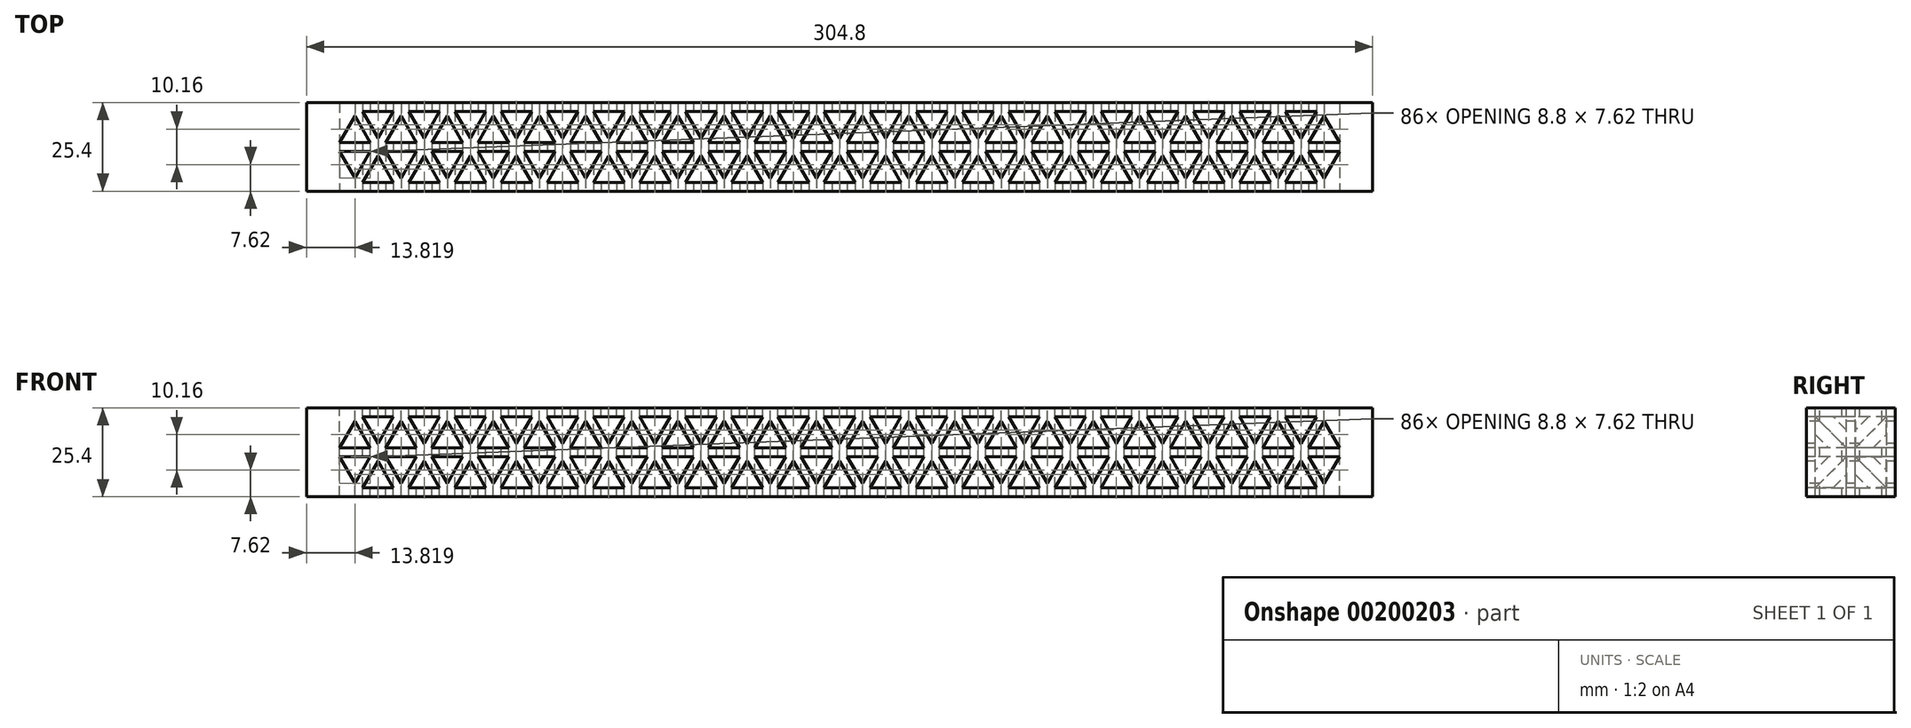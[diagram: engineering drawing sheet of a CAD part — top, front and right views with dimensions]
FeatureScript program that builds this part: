
annotation { "Feature Type Name" : "Feature", "Feature Type Description" : "" }
export const myFeature = defineFeature(function(context is Context, id is Id, definition is map)
    precondition{}
    {
        {
            var Q0;
            Q0=qCreatedBy(makeId("Right.planeOp"),FACE);
            var sketch = newSketch(context, id + "F0", { "sketchPlane" : qUnion([Q0])});
            skLineSegment(sketch, "E0.bottom", {"start": v(12.7, 12.7) * mm, "end": v(-12.7, 12.7) * mm});
            skLineSegment(sketch, "E0.top", {"start": v(12.7, -12.7) * mm, "end": v(-12.7, -12.7) * mm});
            skLineSegment(sketch, "E0.left", {"start": v(12.7, 12.7) * mm, "end": v(12.7, -12.7) * mm});
            skLineSegment(sketch, "E0.right", {"start": v(-12.7, 12.7) * mm, "end": v(-12.7, -12.7) * mm});
            skPoint(sketch, "E0.middle", {"position": v(0, 0) * mm});
            skSolve(sketch);
        }
        {
            var Q0;
            Q0 = qSketchRegion(id + "F0", true);
            extrude(context, id + "F1", {"entities" : qUnion([Q0]), "endBound" : BoundingType.SYMMETRIC, "depth" : 304.8 * mm});
        }
        {
            var Q0;
            Q0=makeQuery(id+"F1.opExtrude","SWEPT_FACE",FACE,{"disambiguationData":[OSD([sQuery(id+"F0.wireOp",EDGE,"E0.right")])]});
            var sketch = newSketch(context, id + "F2", { "sketchPlane" : qUnion([Q0])});
            skCircle(sketch, "E1.cCircle", {"center": v(0, 0) * mm, "radius": 11.43 * mm, "construction": true});
            skLineSegment(sketch, "E1.0", {"start": v(-6.6, 11.43) * mm, "end": v(6.6, 11.43) * mm, "construction": true});
            skLineSegment(sketch, "E1.1", {"start": v(6.6, 11.43) * mm, "end": v(13.2, 0) * mm, "construction": true});
            skLineSegment(sketch, "E1.2", {"start": v(13.2, 0) * mm, "end": v(6.6, -11.43) * mm, "construction": true});
            skLineSegment(sketch, "E1.3", {"start": v(6.6, -11.43) * mm, "end": v(-6.6, -11.43) * mm, "construction": true});
            skLineSegment(sketch, "E1.4", {"start": v(-6.6, -11.43) * mm, "end": v(-13.2, 0) * mm, "construction": true});
            skLineSegment(sketch, "E1.5", {"start": v(-13.2, 0) * mm, "end": v(-6.6, 11.43) * mm, "construction": true});
            skPoint(sketch, "E1.0.midPoint", {"position": v(0, 11.43) * mm});
            skLineSegment(sketch, "E2", {"start": v(6.6, 11.43) * mm, "end": v(-6.6, -11.43) * mm, "construction": true});
            skLineSegment(sketch, "E3", {"start": v(-6.6, 11.43) * mm, "end": v(6.6, -11.43) * mm, "construction": true});
            skLineSegment(sketch, "E4", {"start": v(-13.2, 0) * mm, "end": v(13.2, 0) * mm, "construction": true});
            skLineSegment(sketch, "E5.0", {"start": v(-6.6, -8.9) * mm, "end": v(-11, -1.27) * mm});
            skLineSegment(sketch, "E5.1", {"start": v(-4.4, 10.16) * mm, "end": v(4.4, 10.16) * mm});
            skLineSegment(sketch, "E5.2", {"start": v(6.6, 8.89) * mm, "end": v(11, 1.27) * mm});
            skLineSegment(sketch, "E5.3", {"start": v(-11, 1.27) * mm, "end": v(-6.6, 8.9) * mm});
            skLineSegment(sketch, "E5.4", {"start": v(11, -1.27) * mm, "end": v(6.6, -8.9) * mm});
            skLineSegment(sketch, "E5.5", {"start": v(4.4, -10.16) * mm, "end": v(-4.4, -10.16) * mm});
            skLineSegment(sketch, "E6.0", {"start": v(4.4, 10.16) * mm, "end": v(0, 2.54) * mm});
            skLineSegment(sketch, "E7.0", {"start": v(6.6, 8.9) * mm, "end": v(2.2, 1.27) * mm});
            skLineSegment(sketch, "E8.0", {"start": v(-11, -1.27) * mm, "end": v(-2.2, -1.27) * mm});
            skLineSegment(sketch, "E9.0", {"start": v(-11, 1.27) * mm, "end": v(-2.2, 1.27) * mm});
            skLineSegment(sketch, "E10.trimOffspring", {"start": v(-4.4, 10.16) * mm, "end": v(0, 2.54) * mm});
            skLineSegment(sketch, "E11.trimOffspring", {"start": v(-6.6, 8.9) * mm, "end": v(-2.2, 1.27) * mm});
            skLineSegment(sketch, "E12.trimOffspring", {"start": v(0, -2.54) * mm, "end": v(4.4, -10.16) * mm});
            skLineSegment(sketch, "E13.trimOffspring", {"start": v(2.2, 1.27) * mm, "end": v(11, 1.27) * mm});
            skLineSegment(sketch, "E14.trimOffspring", {"start": v(-2.2, -1.27) * mm, "end": v(-6.6, -8.9) * mm});
            skLineSegment(sketch, "E15.trimOffspring", {"start": v(2.2, -1.27) * mm, "end": v(6.6, -8.9) * mm});
            skLineSegment(sketch, "E16.trimOffspring", {"start": v(0, -2.54) * mm, "end": v(-4.4, -10.16) * mm});
            skLineSegment(sketch, "E17.trimOffspring", {"start": v(2.2, -1.27) * mm, "end": v(11, -1.27) * mm});
            skLineSegment(sketch, "E18.1.0.0", {"start": v(-24.2, 1.27) * mm, "end": v(-19.8, 8.89) * mm});
            skLineSegment(sketch, "E18.1.0.1", {"start": v(-19.8, 8.9) * mm, "end": v(-15.4, 1.27) * mm});
            skLineSegment(sketch, "E18.1.0.2", {"start": v(-24.2, 1.27) * mm, "end": v(-15.4, 1.27) * mm});
            skLineSegment(sketch, "E18.1.0.3", {"start": v(-15.4, -1.27) * mm, "end": v(-19.8, -8.9) * mm});
            skLineSegment(sketch, "E18.1.0.4", {"start": v(-24.2, -1.27) * mm, "end": v(-15.4, -1.27) * mm});
            skLineSegment(sketch, "E18.1.0.5", {"start": v(-19.8, -8.9) * mm, "end": v(-24.2, -1.27) * mm});
            skLineSegment(sketch, "E18.1.0.6", {"start": v(-13.2, -2.54) * mm, "end": v(-8.8, -10.16) * mm});
            skLineSegment(sketch, "E18.1.0.7", {"start": v(-13.2, -2.54) * mm, "end": v(-17.6, -10.16) * mm});
            skLineSegment(sketch, "E18.1.0.8", {"start": v(-8.8, -10.16) * mm, "end": v(-17.6, -10.16) * mm});
            skLineSegment(sketch, "E18.1.0.9", {"start": v(-8.8, 10.16) * mm, "end": v(-13.2, 2.54) * mm});
            skLineSegment(sketch, "E18.1.0.10", {"start": v(-17.6, 10.16) * mm, "end": v(-13.2, 2.54) * mm});
            skLineSegment(sketch, "E18.1.0.11", {"start": v(-17.6, 10.16) * mm, "end": v(-8.8, 10.16) * mm});
            skLineSegment(sketch, "E18.2.0.0", {"start": v(-37.4, 1.27) * mm, "end": v(-33, 8.89) * mm});
            skLineSegment(sketch, "E18.2.0.1", {"start": v(-33, 8.9) * mm, "end": v(-28.6, 1.27) * mm});
            skLineSegment(sketch, "E18.2.0.2", {"start": v(-37.4, 1.27) * mm, "end": v(-28.6, 1.27) * mm});
            skLineSegment(sketch, "E18.2.0.3", {"start": v(-28.6, -1.27) * mm, "end": v(-33, -8.9) * mm});
            skLineSegment(sketch, "E18.2.0.4", {"start": v(-37.4, -1.27) * mm, "end": v(-28.6, -1.27) * mm});
            skLineSegment(sketch, "E18.2.0.5", {"start": v(-33, -8.9) * mm, "end": v(-37.4, -1.27) * mm});
            skLineSegment(sketch, "E18.2.0.6", {"start": v(-26.4, -2.54) * mm, "end": v(-22, -10.16) * mm});
            skLineSegment(sketch, "E18.2.0.7", {"start": v(-26.4, -2.54) * mm, "end": v(-30.8, -10.16) * mm});
            skLineSegment(sketch, "E18.2.0.8", {"start": v(-22, -10.16) * mm, "end": v(-30.8, -10.16) * mm});
            skLineSegment(sketch, "E18.2.0.9", {"start": v(-22, 10.16) * mm, "end": v(-26.4, 2.54) * mm});
            skLineSegment(sketch, "E18.2.0.10", {"start": v(-30.8, 10.16) * mm, "end": v(-26.4, 2.54) * mm});
            skLineSegment(sketch, "E18.2.0.11", {"start": v(-30.8, 10.16) * mm, "end": v(-22, 10.16) * mm});
            skLineSegment(sketch, "E18.direction1", {"start": v(-6.6, -8.9) * mm, "end": v(-19.8, -8.9) * mm, "construction": true});
            skLineSegment(sketch, "E19.0.3.0", {"start": v(-50.6, 1.27) * mm, "end": v(-46.2, 8.9) * mm});
            skLineSegment(sketch, "E19.3.3.0", {"start": v(-46.2, 8.9) * mm, "end": v(-41.8, 1.27) * mm});
            skLineSegment(sketch, "E19.6.3.0", {"start": v(-50.6, 1.27) * mm, "end": v(-41.8, 1.27) * mm});
            skLineSegment(sketch, "E19.9.3.0", {"start": v(-41.8, -1.27) * mm, "end": v(-46.2, -8.9) * mm});
            skLineSegment(sketch, "E19.12.3.0", {"start": v(-50.6, -1.27) * mm, "end": v(-41.8, -1.27) * mm});
            skLineSegment(sketch, "E19.15.3.0", {"start": v(-46.2, -8.9) * mm, "end": v(-50.6, -1.27) * mm});
            skLineSegment(sketch, "E19.18.3.0", {"start": v(-39.6, -2.54) * mm, "end": v(-35.2, -10.16) * mm});
            skLineSegment(sketch, "E19.21.3.0", {"start": v(-39.6, -2.54) * mm, "end": v(-44, -10.16) * mm});
            skLineSegment(sketch, "E19.24.3.0", {"start": v(-35.2, -10.16) * mm, "end": v(-44, -10.16) * mm});
            skLineSegment(sketch, "E19.27.3.0", {"start": v(-35.2, 10.16) * mm, "end": v(-39.6, 2.54) * mm});
            skLineSegment(sketch, "E19.30.3.0", {"start": v(-44, 10.16) * mm, "end": v(-39.6, 2.54) * mm});
            skLineSegment(sketch, "E19.33.3.0", {"start": v(-44, 10.16) * mm, "end": v(-35.2, 10.16) * mm});
            skLineSegment(sketch, "E19.0.4.0", {"start": v(-63.8, 1.27) * mm, "end": v(-59.4, 8.9) * mm});
            skLineSegment(sketch, "E19.3.4.0", {"start": v(-59.4, 8.9) * mm, "end": v(-55, 1.27) * mm});
            skLineSegment(sketch, "E19.6.4.0", {"start": v(-63.8, 1.27) * mm, "end": v(-55, 1.27) * mm});
            skLineSegment(sketch, "E19.9.4.0", {"start": v(-55, -1.27) * mm, "end": v(-59.4, -8.9) * mm});
            skLineSegment(sketch, "E19.12.4.0", {"start": v(-63.8, -1.27) * mm, "end": v(-55, -1.27) * mm});
            skLineSegment(sketch, "E19.15.4.0", {"start": v(-59.4, -8.9) * mm, "end": v(-63.8, -1.27) * mm});
            skLineSegment(sketch, "E19.18.4.0", {"start": v(-52.8, -2.54) * mm, "end": v(-48.4, -10.16) * mm});
            skLineSegment(sketch, "E19.21.4.0", {"start": v(-52.8, -2.54) * mm, "end": v(-57.2, -10.16) * mm});
            skLineSegment(sketch, "E19.24.4.0", {"start": v(-48.4, -10.16) * mm, "end": v(-57.2, -10.16) * mm});
            skLineSegment(sketch, "E19.27.4.0", {"start": v(-48.4, 10.16) * mm, "end": v(-52.8, 2.54) * mm});
            skLineSegment(sketch, "E19.30.4.0", {"start": v(-57.2, 10.16) * mm, "end": v(-52.8, 2.54) * mm});
            skLineSegment(sketch, "E19.33.4.0", {"start": v(-57.2, 10.16) * mm, "end": v(-48.4, 10.16) * mm});
            skLineSegment(sketch, "E20.0.5.0", {"start": v(-76.99, 1.27) * mm, "end": v(-72.6, 8.9) * mm});
            skLineSegment(sketch, "E20.3.5.0", {"start": v(-72.6, 8.9) * mm, "end": v(-68.2, 1.27) * mm});
            skLineSegment(sketch, "E20.6.5.0", {"start": v(-76.99, 1.27) * mm, "end": v(-68.2, 1.27) * mm});
            skLineSegment(sketch, "E20.9.5.0", {"start": v(-68.2, -1.27) * mm, "end": v(-72.6, -8.9) * mm});
            skLineSegment(sketch, "E20.12.5.0", {"start": v(-76.99, -1.27) * mm, "end": v(-68.2, -1.27) * mm});
            skLineSegment(sketch, "E20.15.5.0", {"start": v(-72.6, -8.9) * mm, "end": v(-76.99, -1.27) * mm});
            skLineSegment(sketch, "E20.18.5.0", {"start": v(-66, -2.54) * mm, "end": v(-61.6, -10.16) * mm});
            skLineSegment(sketch, "E20.21.5.0", {"start": v(-66, -2.54) * mm, "end": v(-70.4, -10.16) * mm});
            skLineSegment(sketch, "E20.24.5.0", {"start": v(-61.6, -10.16) * mm, "end": v(-70.4, -10.16) * mm});
            skLineSegment(sketch, "E20.27.5.0", {"start": v(-61.6, 10.16) * mm, "end": v(-66, 2.54) * mm});
            skLineSegment(sketch, "E20.30.5.0", {"start": v(-70.4, 10.16) * mm, "end": v(-66, 2.54) * mm});
            skLineSegment(sketch, "E20.33.5.0", {"start": v(-70.4, 10.16) * mm, "end": v(-61.6, 10.16) * mm});
            skLineSegment(sketch, "E20.0.6.0", {"start": v(-90.19, 1.27) * mm, "end": v(-85.79, 8.9) * mm});
            skLineSegment(sketch, "E20.3.6.0", {"start": v(-85.79, 8.9) * mm, "end": v(-81.39, 1.27) * mm});
            skLineSegment(sketch, "E20.6.6.0", {"start": v(-90.19, 1.27) * mm, "end": v(-81.39, 1.27) * mm});
            skLineSegment(sketch, "E20.9.6.0", {"start": v(-81.39, -1.27) * mm, "end": v(-85.79, -8.9) * mm});
            skLineSegment(sketch, "E20.12.6.0", {"start": v(-90.19, -1.27) * mm, "end": v(-81.39, -1.27) * mm});
            skLineSegment(sketch, "E20.15.6.0", {"start": v(-85.79, -8.9) * mm, "end": v(-90.19, -1.27) * mm});
            skLineSegment(sketch, "E20.18.6.0", {"start": v(-79.19, -2.54) * mm, "end": v(-74.79, -10.16) * mm});
            skLineSegment(sketch, "E20.21.6.0", {"start": v(-79.19, -2.54) * mm, "end": v(-83.59, -10.16) * mm});
            skLineSegment(sketch, "E20.24.6.0", {"start": v(-74.79, -10.16) * mm, "end": v(-83.59, -10.16) * mm});
            skLineSegment(sketch, "E20.27.6.0", {"start": v(-74.79, 10.16) * mm, "end": v(-79.19, 2.54) * mm});
            skLineSegment(sketch, "E20.30.6.0", {"start": v(-83.59, 10.16) * mm, "end": v(-79.19, 2.54) * mm});
            skLineSegment(sketch, "E20.33.6.0", {"start": v(-83.59, 10.16) * mm, "end": v(-74.79, 10.16) * mm});
            skLineSegment(sketch, "E20.0.7.0", {"start": v(-103.39, 1.27) * mm, "end": v(-98.99, 8.9) * mm});
            skLineSegment(sketch, "E20.3.7.0", {"start": v(-98.99, 8.9) * mm, "end": v(-94.59, 1.27) * mm});
            skLineSegment(sketch, "E20.6.7.0", {"start": v(-103.39, 1.27) * mm, "end": v(-94.59, 1.27) * mm});
            skLineSegment(sketch, "E20.9.7.0", {"start": v(-94.59, -1.27) * mm, "end": v(-98.99, -8.9) * mm});
            skLineSegment(sketch, "E20.12.7.0", {"start": v(-103.39, -1.27) * mm, "end": v(-94.59, -1.27) * mm});
            skLineSegment(sketch, "E20.15.7.0", {"start": v(-98.99, -8.9) * mm, "end": v(-103.39, -1.27) * mm});
            skLineSegment(sketch, "E20.18.7.0", {"start": v(-92.39, -2.54) * mm, "end": v(-87.99, -10.16) * mm});
            skLineSegment(sketch, "E20.21.7.0", {"start": v(-92.39, -2.54) * mm, "end": v(-96.79, -10.16) * mm});
            skLineSegment(sketch, "E20.24.7.0", {"start": v(-87.99, -10.16) * mm, "end": v(-96.79, -10.16) * mm});
            skLineSegment(sketch, "E20.27.7.0", {"start": v(-87.99, 10.16) * mm, "end": v(-92.39, 2.54) * mm});
            skLineSegment(sketch, "E20.30.7.0", {"start": v(-96.79, 10.16) * mm, "end": v(-92.39, 2.54) * mm});
            skLineSegment(sketch, "E20.33.7.0", {"start": v(-96.79, 10.16) * mm, "end": v(-87.99, 10.16) * mm});
            skLineSegment(sketch, "E20.0.8.0", {"start": v(-116.58, 1.27) * mm, "end": v(-112.18, 8.9) * mm});
            skLineSegment(sketch, "E20.3.8.0", {"start": v(-112.18, 8.9) * mm, "end": v(-107.79, 1.27) * mm});
            skLineSegment(sketch, "E20.6.8.0", {"start": v(-116.58, 1.27) * mm, "end": v(-107.79, 1.27) * mm});
            skLineSegment(sketch, "E20.9.8.0", {"start": v(-107.79, -1.27) * mm, "end": v(-112.18, -8.9) * mm});
            skLineSegment(sketch, "E20.12.8.0", {"start": v(-116.58, -1.27) * mm, "end": v(-107.79, -1.27) * mm});
            skLineSegment(sketch, "E20.15.8.0", {"start": v(-112.18, -8.9) * mm, "end": v(-116.58, -1.27) * mm});
            skLineSegment(sketch, "E20.18.8.0", {"start": v(-105.59, -2.54) * mm, "end": v(-101.19, -10.16) * mm});
            skLineSegment(sketch, "E20.21.8.0", {"start": v(-105.59, -2.54) * mm, "end": v(-109.99, -10.16) * mm});
            skLineSegment(sketch, "E20.24.8.0", {"start": v(-101.19, -10.16) * mm, "end": v(-109.99, -10.16) * mm});
            skLineSegment(sketch, "E20.27.8.0", {"start": v(-101.19, 10.16) * mm, "end": v(-105.59, 2.54) * mm});
            skLineSegment(sketch, "E20.30.8.0", {"start": v(-109.99, 10.16) * mm, "end": v(-105.59, 2.54) * mm});
            skLineSegment(sketch, "E20.33.8.0", {"start": v(-109.99, 10.16) * mm, "end": v(-101.19, 10.16) * mm});
            skLineSegment(sketch, "E20.0.9.0", {"start": v(-129.78, 1.27) * mm, "end": v(-125.38, 8.9) * mm});
            skLineSegment(sketch, "E20.3.9.0", {"start": v(-125.38, 8.9) * mm, "end": v(-120.98, 1.27) * mm});
            skLineSegment(sketch, "E20.6.9.0", {"start": v(-129.78, 1.27) * mm, "end": v(-120.98, 1.27) * mm});
            skLineSegment(sketch, "E20.9.9.0", {"start": v(-120.98, -1.27) * mm, "end": v(-125.38, -8.9) * mm});
            skLineSegment(sketch, "E20.12.9.0", {"start": v(-129.78, -1.27) * mm, "end": v(-120.98, -1.27) * mm});
            skLineSegment(sketch, "E20.15.9.0", {"start": v(-125.38, -8.9) * mm, "end": v(-129.78, -1.27) * mm});
            skLineSegment(sketch, "E20.18.9.0", {"start": v(-118.78, -2.54) * mm, "end": v(-114.38, -10.16) * mm});
            skLineSegment(sketch, "E20.21.9.0", {"start": v(-118.78, -2.54) * mm, "end": v(-123.18, -10.16) * mm});
            skLineSegment(sketch, "E20.24.9.0", {"start": v(-114.38, -10.16) * mm, "end": v(-123.18, -10.16) * mm});
            skLineSegment(sketch, "E20.27.9.0", {"start": v(-114.38, 10.16) * mm, "end": v(-118.78, 2.54) * mm});
            skLineSegment(sketch, "E20.30.9.0", {"start": v(-123.18, 10.16) * mm, "end": v(-118.78, 2.54) * mm});
            skLineSegment(sketch, "E20.33.9.0", {"start": v(-123.18, 10.16) * mm, "end": v(-114.38, 10.16) * mm});
            skLineSegment(sketch, "E21.0.10.0", {"start": v(-142.98, 1.27) * mm, "end": v(-138.58, 8.9) * mm});
            skLineSegment(sketch, "E21.3.10.0", {"start": v(-138.58, 8.9) * mm, "end": v(-134.18, 1.27) * mm});
            skLineSegment(sketch, "E21.6.10.0", {"start": v(-142.98, 1.27) * mm, "end": v(-134.18, 1.27) * mm});
            skLineSegment(sketch, "E21.9.10.0", {"start": v(-134.18, -1.27) * mm, "end": v(-138.58, -8.9) * mm});
            skLineSegment(sketch, "E21.12.10.0", {"start": v(-142.98, -1.27) * mm, "end": v(-134.18, -1.27) * mm});
            skLineSegment(sketch, "E21.15.10.0", {"start": v(-138.58, -8.9) * mm, "end": v(-142.98, -1.27) * mm});
            skLineSegment(sketch, "E21.18.10.0", {"start": v(-131.98, -2.54) * mm, "end": v(-127.58, -10.16) * mm});
            skLineSegment(sketch, "E21.21.10.0", {"start": v(-131.98, -2.54) * mm, "end": v(-136.38, -10.16) * mm});
            skLineSegment(sketch, "E21.24.10.0", {"start": v(-127.58, -10.16) * mm, "end": v(-136.38, -10.16) * mm});
            skLineSegment(sketch, "E21.27.10.0", {"start": v(-127.58, 10.16) * mm, "end": v(-131.98, 2.54) * mm});
            skLineSegment(sketch, "E21.30.10.0", {"start": v(-136.38, 10.16) * mm, "end": v(-131.98, 2.54) * mm});
            skLineSegment(sketch, "E21.33.10.0", {"start": v(-136.38, 10.16) * mm, "end": v(-127.58, 10.16) * mm});
            skLineSegment(sketch, "E22.1.0.0", {"start": v(8.8, 10.16) * mm, "end": v(17.6, 10.16) * mm});
            skLineSegment(sketch, "E22.1.0.1", {"start": v(17.6, 10.16) * mm, "end": v(13.2, 2.54) * mm});
            skLineSegment(sketch, "E22.1.0.2", {"start": v(8.8, 10.16) * mm, "end": v(13.2, 2.54) * mm});
            skLineSegment(sketch, "E22.1.0.3", {"start": v(13.2, -2.54) * mm, "end": v(17.6, -10.16) * mm});
            skLineSegment(sketch, "E22.1.0.4", {"start": v(13.2, -2.54) * mm, "end": v(8.8, -10.16) * mm});
            skLineSegment(sketch, "E22.1.0.5", {"start": v(17.6, -10.16) * mm, "end": v(8.8, -10.16) * mm});
            skLineSegment(sketch, "E22.1.0.6", {"start": v(24.2, -1.27) * mm, "end": v(19.8, -8.9) * mm});
            skLineSegment(sketch, "E22.1.0.7", {"start": v(15.4, -1.27) * mm, "end": v(19.8, -8.9) * mm});
            skLineSegment(sketch, "E22.1.0.8", {"start": v(15.4, -1.27) * mm, "end": v(24.2, -1.27) * mm});
            skLineSegment(sketch, "E22.1.0.9", {"start": v(15.4, 1.27) * mm, "end": v(24.2, 1.27) * mm});
            skLineSegment(sketch, "E22.1.0.10", {"start": v(19.8, 8.89) * mm, "end": v(24.2, 1.27) * mm});
            skLineSegment(sketch, "E22.1.0.11", {"start": v(19.8, 8.89) * mm, "end": v(15.4, 1.27) * mm});
            skLineSegment(sketch, "E22.2.0.0", {"start": v(22, 10.16) * mm, "end": v(30.8, 10.16) * mm});
            skLineSegment(sketch, "E22.2.0.1", {"start": v(30.8, 10.16) * mm, "end": v(26.4, 2.54) * mm});
            skLineSegment(sketch, "E22.2.0.2", {"start": v(22, 10.16) * mm, "end": v(26.4, 2.54) * mm});
            skLineSegment(sketch, "E22.2.0.3", {"start": v(26.4, -2.54) * mm, "end": v(30.8, -10.16) * mm});
            skLineSegment(sketch, "E22.2.0.4", {"start": v(26.4, -2.54) * mm, "end": v(22, -10.16) * mm});
            skLineSegment(sketch, "E22.2.0.5", {"start": v(30.8, -10.16) * mm, "end": v(22, -10.16) * mm});
            skLineSegment(sketch, "E22.2.0.6", {"start": v(37.4, -1.27) * mm, "end": v(33, -8.9) * mm});
            skLineSegment(sketch, "E22.2.0.7", {"start": v(28.6, -1.27) * mm, "end": v(33, -8.9) * mm});
            skLineSegment(sketch, "E22.2.0.8", {"start": v(28.6, -1.27) * mm, "end": v(37.4, -1.27) * mm});
            skLineSegment(sketch, "E22.2.0.9", {"start": v(28.6, 1.27) * mm, "end": v(37.4, 1.27) * mm});
            skLineSegment(sketch, "E22.2.0.10", {"start": v(33, 8.89) * mm, "end": v(37.4, 1.27) * mm});
            skLineSegment(sketch, "E22.2.0.11", {"start": v(33, 8.89) * mm, "end": v(28.6, 1.27) * mm});
            skLineSegment(sketch, "E22.3.0.0", {"start": v(35.2, 10.16) * mm, "end": v(44, 10.16) * mm});
            skLineSegment(sketch, "E22.3.0.1", {"start": v(44, 10.16) * mm, "end": v(39.6, 2.54) * mm});
            skLineSegment(sketch, "E22.3.0.2", {"start": v(35.2, 10.16) * mm, "end": v(39.6, 2.54) * mm});
            skLineSegment(sketch, "E22.3.0.3", {"start": v(39.6, -2.54) * mm, "end": v(44, -10.16) * mm});
            skLineSegment(sketch, "E22.3.0.4", {"start": v(39.6, -2.54) * mm, "end": v(35.2, -10.16) * mm});
            skLineSegment(sketch, "E22.3.0.5", {"start": v(44, -10.16) * mm, "end": v(35.2, -10.16) * mm});
            skLineSegment(sketch, "E22.3.0.6", {"start": v(50.6, -1.27) * mm, "end": v(46.2, -8.9) * mm});
            skLineSegment(sketch, "E22.3.0.7", {"start": v(41.8, -1.27) * mm, "end": v(46.2, -8.9) * mm});
            skLineSegment(sketch, "E22.3.0.8", {"start": v(41.8, -1.27) * mm, "end": v(50.6, -1.27) * mm});
            skLineSegment(sketch, "E22.3.0.9", {"start": v(41.8, 1.27) * mm, "end": v(50.6, 1.27) * mm});
            skLineSegment(sketch, "E22.3.0.10", {"start": v(46.2, 8.89) * mm, "end": v(50.6, 1.27) * mm});
            skLineSegment(sketch, "E22.3.0.11", {"start": v(46.2, 8.89) * mm, "end": v(41.8, 1.27) * mm});
            skLineSegment(sketch, "E22.4.0.0", {"start": v(48.4, 10.16) * mm, "end": v(57.2, 10.16) * mm});
            skLineSegment(sketch, "E22.4.0.1", {"start": v(57.2, 10.16) * mm, "end": v(52.8, 2.54) * mm});
            skLineSegment(sketch, "E22.4.0.2", {"start": v(48.4, 10.16) * mm, "end": v(52.8, 2.54) * mm});
            skLineSegment(sketch, "E22.4.0.3", {"start": v(52.8, -2.54) * mm, "end": v(57.2, -10.16) * mm});
            skLineSegment(sketch, "E22.4.0.4", {"start": v(52.8, -2.54) * mm, "end": v(48.4, -10.16) * mm});
            skLineSegment(sketch, "E22.4.0.5", {"start": v(57.2, -10.16) * mm, "end": v(48.4, -10.16) * mm});
            skLineSegment(sketch, "E22.4.0.6", {"start": v(63.8, -1.27) * mm, "end": v(59.4, -8.9) * mm});
            skLineSegment(sketch, "E22.4.0.7", {"start": v(55, -1.27) * mm, "end": v(59.4, -8.9) * mm});
            skLineSegment(sketch, "E22.4.0.8", {"start": v(55, -1.27) * mm, "end": v(63.8, -1.27) * mm});
            skLineSegment(sketch, "E22.4.0.9", {"start": v(55, 1.27) * mm, "end": v(63.8, 1.27) * mm});
            skLineSegment(sketch, "E22.4.0.10", {"start": v(59.4, 8.89) * mm, "end": v(63.8, 1.27) * mm});
            skLineSegment(sketch, "E22.4.0.11", {"start": v(59.4, 8.89) * mm, "end": v(55, 1.27) * mm});
            skLineSegment(sketch, "E22.5.0.0", {"start": v(61.6, 10.16) * mm, "end": v(70.4, 10.16) * mm});
            skLineSegment(sketch, "E22.5.0.1", {"start": v(70.4, 10.16) * mm, "end": v(66, 2.54) * mm});
            skLineSegment(sketch, "E22.5.0.2", {"start": v(61.6, 10.16) * mm, "end": v(66, 2.54) * mm});
            skLineSegment(sketch, "E22.5.0.3", {"start": v(66, -2.54) * mm, "end": v(70.4, -10.16) * mm});
            skLineSegment(sketch, "E22.5.0.4", {"start": v(66, -2.54) * mm, "end": v(61.6, -10.16) * mm});
            skLineSegment(sketch, "E22.5.0.5", {"start": v(70.4, -10.16) * mm, "end": v(61.6, -10.16) * mm});
            skLineSegment(sketch, "E22.5.0.6", {"start": v(76.99, -1.27) * mm, "end": v(72.6, -8.9) * mm});
            skLineSegment(sketch, "E22.5.0.7", {"start": v(68.2, -1.27) * mm, "end": v(72.6, -8.9) * mm});
            skLineSegment(sketch, "E22.5.0.8", {"start": v(68.2, -1.27) * mm, "end": v(76.99, -1.27) * mm});
            skLineSegment(sketch, "E22.5.0.9", {"start": v(68.2, 1.27) * mm, "end": v(76.99, 1.27) * mm});
            skLineSegment(sketch, "E22.5.0.10", {"start": v(72.6, 8.89) * mm, "end": v(76.99, 1.27) * mm});
            skLineSegment(sketch, "E22.5.0.11", {"start": v(72.6, 8.89) * mm, "end": v(68.2, 1.27) * mm});
            skLineSegment(sketch, "E22.6.0.0", {"start": v(74.79, 10.16) * mm, "end": v(83.59, 10.16) * mm});
            skLineSegment(sketch, "E22.6.0.1", {"start": v(83.59, 10.16) * mm, "end": v(79.19, 2.54) * mm});
            skLineSegment(sketch, "E22.6.0.2", {"start": v(74.79, 10.16) * mm, "end": v(79.19, 2.54) * mm});
            skLineSegment(sketch, "E22.6.0.3", {"start": v(79.19, -2.54) * mm, "end": v(83.59, -10.16) * mm});
            skLineSegment(sketch, "E22.6.0.4", {"start": v(79.19, -2.54) * mm, "end": v(74.79, -10.16) * mm});
            skLineSegment(sketch, "E22.6.0.5", {"start": v(83.59, -10.16) * mm, "end": v(74.79, -10.16) * mm});
            skLineSegment(sketch, "E22.6.0.6", {"start": v(90.19, -1.27) * mm, "end": v(85.79, -8.9) * mm});
            skLineSegment(sketch, "E22.6.0.7", {"start": v(81.39, -1.27) * mm, "end": v(85.79, -8.9) * mm});
            skLineSegment(sketch, "E22.6.0.8", {"start": v(81.39, -1.27) * mm, "end": v(90.19, -1.27) * mm});
            skLineSegment(sketch, "E22.6.0.9", {"start": v(81.39, 1.27) * mm, "end": v(90.19, 1.27) * mm});
            skLineSegment(sketch, "E22.6.0.10", {"start": v(85.79, 8.89) * mm, "end": v(90.19, 1.27) * mm});
            skLineSegment(sketch, "E22.6.0.11", {"start": v(85.79, 8.89) * mm, "end": v(81.39, 1.27) * mm});
            skLineSegment(sketch, "E22.7.0.0", {"start": v(87.99, 10.16) * mm, "end": v(96.79, 10.16) * mm});
            skLineSegment(sketch, "E22.7.0.1", {"start": v(96.79, 10.16) * mm, "end": v(92.39, 2.54) * mm});
            skLineSegment(sketch, "E22.7.0.2", {"start": v(87.99, 10.16) * mm, "end": v(92.39, 2.54) * mm});
            skLineSegment(sketch, "E22.7.0.3", {"start": v(92.39, -2.54) * mm, "end": v(96.79, -10.16) * mm});
            skLineSegment(sketch, "E22.7.0.4", {"start": v(92.39, -2.54) * mm, "end": v(87.99, -10.16) * mm});
            skLineSegment(sketch, "E22.7.0.5", {"start": v(96.79, -10.16) * mm, "end": v(87.99, -10.16) * mm});
            skLineSegment(sketch, "E22.7.0.6", {"start": v(103.39, -1.27) * mm, "end": v(98.99, -8.9) * mm});
            skLineSegment(sketch, "E22.7.0.7", {"start": v(94.59, -1.27) * mm, "end": v(98.99, -8.9) * mm});
            skLineSegment(sketch, "E22.7.0.8", {"start": v(94.59, -1.27) * mm, "end": v(103.39, -1.27) * mm});
            skLineSegment(sketch, "E22.7.0.9", {"start": v(94.59, 1.27) * mm, "end": v(103.39, 1.27) * mm});
            skLineSegment(sketch, "E22.7.0.10", {"start": v(98.99, 8.89) * mm, "end": v(103.39, 1.27) * mm});
            skLineSegment(sketch, "E22.7.0.11", {"start": v(98.99, 8.9) * mm, "end": v(94.59, 1.27) * mm});
            skLineSegment(sketch, "E22.8.0.0", {"start": v(101.19, 10.16) * mm, "end": v(109.99, 10.16) * mm});
            skLineSegment(sketch, "E22.8.0.1", {"start": v(109.99, 10.16) * mm, "end": v(105.59, 2.54) * mm});
            skLineSegment(sketch, "E22.8.0.2", {"start": v(101.19, 10.16) * mm, "end": v(105.59, 2.54) * mm});
            skLineSegment(sketch, "E22.8.0.3", {"start": v(105.59, -2.54) * mm, "end": v(109.99, -10.16) * mm});
            skLineSegment(sketch, "E22.8.0.4", {"start": v(105.59, -2.54) * mm, "end": v(101.19, -10.16) * mm});
            skLineSegment(sketch, "E22.8.0.5", {"start": v(109.99, -10.16) * mm, "end": v(101.19, -10.16) * mm});
            skLineSegment(sketch, "E22.8.0.6", {"start": v(116.58, -1.27) * mm, "end": v(112.18, -8.9) * mm});
            skLineSegment(sketch, "E22.8.0.7", {"start": v(107.79, -1.27) * mm, "end": v(112.18, -8.9) * mm});
            skLineSegment(sketch, "E22.8.0.8", {"start": v(107.79, -1.27) * mm, "end": v(116.58, -1.27) * mm});
            skLineSegment(sketch, "E22.8.0.9", {"start": v(107.79, 1.27) * mm, "end": v(116.58, 1.27) * mm});
            skLineSegment(sketch, "E22.8.0.10", {"start": v(112.18, 8.89) * mm, "end": v(116.58, 1.27) * mm});
            skLineSegment(sketch, "E22.8.0.11", {"start": v(112.18, 8.9) * mm, "end": v(107.79, 1.27) * mm});
            skLineSegment(sketch, "E22.9.0.0", {"start": v(114.38, 10.16) * mm, "end": v(123.18, 10.16) * mm});
            skLineSegment(sketch, "E22.9.0.1", {"start": v(123.18, 10.16) * mm, "end": v(118.78, 2.54) * mm});
            skLineSegment(sketch, "E22.9.0.2", {"start": v(114.38, 10.16) * mm, "end": v(118.78, 2.54) * mm});
            skLineSegment(sketch, "E22.9.0.3", {"start": v(118.78, -2.54) * mm, "end": v(123.18, -10.16) * mm});
            skLineSegment(sketch, "E22.9.0.4", {"start": v(118.78, -2.54) * mm, "end": v(114.38, -10.16) * mm});
            skLineSegment(sketch, "E22.9.0.5", {"start": v(123.18, -10.16) * mm, "end": v(114.38, -10.16) * mm});
            skLineSegment(sketch, "E22.9.0.6", {"start": v(129.78, -1.27) * mm, "end": v(125.38, -8.9) * mm});
            skLineSegment(sketch, "E22.9.0.7", {"start": v(120.98, -1.27) * mm, "end": v(125.38, -8.9) * mm});
            skLineSegment(sketch, "E22.9.0.8", {"start": v(120.98, -1.27) * mm, "end": v(129.78, -1.27) * mm});
            skLineSegment(sketch, "E22.9.0.9", {"start": v(120.98, 1.27) * mm, "end": v(129.78, 1.27) * mm});
            skLineSegment(sketch, "E22.9.0.10", {"start": v(125.38, 8.89) * mm, "end": v(129.78, 1.27) * mm});
            skLineSegment(sketch, "E22.9.0.11", {"start": v(125.38, 8.89) * mm, "end": v(120.98, 1.27) * mm});
            skLineSegment(sketch, "E22.10.0.0", {"start": v(127.58, 10.16) * mm, "end": v(136.38, 10.16) * mm});
            skLineSegment(sketch, "E22.10.0.1", {"start": v(136.38, 10.16) * mm, "end": v(131.98, 2.54) * mm});
            skLineSegment(sketch, "E22.10.0.2", {"start": v(127.58, 10.16) * mm, "end": v(131.98, 2.54) * mm});
            skLineSegment(sketch, "E22.10.0.3", {"start": v(131.98, -2.54) * mm, "end": v(136.38, -10.16) * mm});
            skLineSegment(sketch, "E22.10.0.4", {"start": v(131.98, -2.54) * mm, "end": v(127.58, -10.16) * mm});
            skLineSegment(sketch, "E22.10.0.5", {"start": v(136.38, -10.16) * mm, "end": v(127.58, -10.16) * mm});
            skLineSegment(sketch, "E22.10.0.6", {"start": v(142.98, -1.27) * mm, "end": v(138.58, -8.9) * mm});
            skLineSegment(sketch, "E22.10.0.7", {"start": v(134.18, -1.27) * mm, "end": v(138.58, -8.9) * mm});
            skLineSegment(sketch, "E22.10.0.8", {"start": v(134.18, -1.27) * mm, "end": v(142.98, -1.27) * mm});
            skLineSegment(sketch, "E22.10.0.9", {"start": v(134.18, 1.27) * mm, "end": v(142.98, 1.27) * mm});
            skLineSegment(sketch, "E22.10.0.10", {"start": v(138.58, 8.89) * mm, "end": v(142.98, 1.27) * mm});
            skLineSegment(sketch, "E22.10.0.11", {"start": v(138.58, 8.89) * mm, "end": v(134.18, 1.27) * mm});
            skLineSegment(sketch, "E22.direction1", {"start": v(-4.4, -10.16) * mm, "end": v(8.8, -10.16) * mm, "construction": true});
            skSolve(sketch);
        }
        {
            var Q0;
            Q0 = qSketchRegion(id + "F2", true);
            extrude(context, id + "F3", {"entities" : qUnion([Q0]), "operationType" : NewBodyOperationType.REMOVE, "endBound" : BoundingType.THROUGH_ALL, "oppositeDirection" : true, "depth" : 25.4 * mm});
        }
        {
            var Q0;
            Q0 = qSketchRegion(id + "F2", true);
            extrude(context, id + "F4", {"entities" : qUnion([Q0]), "depth" : 25.4 * mm});
        }
        {
            var Q0;
            Q0=makeQuery(id+"F4.opExtrude","SWEPT_BODY",BODY,{"disambiguationData":[OSD([sQuery(id+"F2.wireOp",EDGE,"E22.10.0.9"),sQuery(id+"F2.wireOp",EDGE,"E22.10.0.10"),sQuery(id+"F2.wireOp",EDGE,"E22.10.0.11")])]});
            var Q1;
            Q1=makeQuery(id+"F4.opExtrude","SWEPT_BODY",BODY,{"disambiguationData":[OSD([sQuery(id+"F2.wireOp",EDGE,"E22.10.0.0"),sQuery(id+"F2.wireOp",EDGE,"E22.10.0.1"),sQuery(id+"F2.wireOp",EDGE,"E22.10.0.2")])]});
            var Q2;
            Q2=makeQuery(id+"F4.opExtrude","SWEPT_BODY",BODY,{"disambiguationData":[OSD([sQuery(id+"F2.wireOp",EDGE,"E22.9.0.9"),sQuery(id+"F2.wireOp",EDGE,"E22.9.0.10"),sQuery(id+"F2.wireOp",EDGE,"E22.9.0.11")])]});
            var Q3;
            Q3=makeQuery(id+"F4.opExtrude","SWEPT_BODY",BODY,{"disambiguationData":[OSD([sQuery(id+"F2.wireOp",EDGE,"E22.9.0.0"),sQuery(id+"F2.wireOp",EDGE,"E22.9.0.1"),sQuery(id+"F2.wireOp",EDGE,"E22.9.0.2")])]});
            var Q4;
            Q4=makeQuery(id+"F4.opExtrude","SWEPT_BODY",BODY,{"disambiguationData":[OSD([sQuery(id+"F2.wireOp",EDGE,"E22.8.0.9"),sQuery(id+"F2.wireOp",EDGE,"E22.8.0.10"),sQuery(id+"F2.wireOp",EDGE,"E22.8.0.11")])]});
            var Q5;
            Q5=makeQuery(id+"F4.opExtrude","SWEPT_BODY",BODY,{"disambiguationData":[OSD([sQuery(id+"F2.wireOp",EDGE,"E22.8.0.0"),sQuery(id+"F2.wireOp",EDGE,"E22.8.0.1"),sQuery(id+"F2.wireOp",EDGE,"E22.8.0.2")])]});
            var Q6;
            Q6=makeQuery(id+"F4.opExtrude","SWEPT_BODY",BODY,{"disambiguationData":[OSD([sQuery(id+"F2.wireOp",EDGE,"E22.7.0.9"),sQuery(id+"F2.wireOp",EDGE,"E22.7.0.10"),sQuery(id+"F2.wireOp",EDGE,"E22.7.0.11")])]});
            var Q7;
            Q7=makeQuery(id+"F4.opExtrude","SWEPT_BODY",BODY,{"disambiguationData":[OSD([sQuery(id+"F2.wireOp",EDGE,"E22.7.0.0"),sQuery(id+"F2.wireOp",EDGE,"E22.7.0.1"),sQuery(id+"F2.wireOp",EDGE,"E22.7.0.2")])]});
            var Q8;
            Q8=makeQuery(id+"F4.opExtrude","SWEPT_BODY",BODY,{"disambiguationData":[OSD([sQuery(id+"F2.wireOp",EDGE,"E22.6.0.9"),sQuery(id+"F2.wireOp",EDGE,"E22.6.0.10"),sQuery(id+"F2.wireOp",EDGE,"E22.6.0.11")])]});
            var Q9;
            Q9=makeQuery(id+"F4.opExtrude","SWEPT_BODY",BODY,{"disambiguationData":[OSD([sQuery(id+"F2.wireOp",EDGE,"E22.6.0.0"),sQuery(id+"F2.wireOp",EDGE,"E22.6.0.1"),sQuery(id+"F2.wireOp",EDGE,"E22.6.0.2")])]});
            var Q10;
            Q10=makeQuery(id+"F4.opExtrude","SWEPT_BODY",BODY,{"disambiguationData":[OSD([sQuery(id+"F2.wireOp",EDGE,"E22.5.0.9"),sQuery(id+"F2.wireOp",EDGE,"E22.5.0.10"),sQuery(id+"F2.wireOp",EDGE,"E22.5.0.11")])]});
            var Q11;
            Q11=makeQuery(id+"F4.opExtrude","SWEPT_BODY",BODY,{"disambiguationData":[OSD([sQuery(id+"F2.wireOp",EDGE,"E22.5.0.0"),sQuery(id+"F2.wireOp",EDGE,"E22.5.0.1"),sQuery(id+"F2.wireOp",EDGE,"E22.5.0.2")])]});
            var Q12;
            Q12=makeQuery(id+"F4.opExtrude","SWEPT_BODY",BODY,{"disambiguationData":[OSD([sQuery(id+"F2.wireOp",EDGE,"E22.4.0.9"),sQuery(id+"F2.wireOp",EDGE,"E22.4.0.10"),sQuery(id+"F2.wireOp",EDGE,"E22.4.0.11")])]});
            var Q13;
            Q13=makeQuery(id+"F4.opExtrude","SWEPT_BODY",BODY,{"disambiguationData":[OSD([sQuery(id+"F2.wireOp",EDGE,"E22.4.0.0"),sQuery(id+"F2.wireOp",EDGE,"E22.4.0.1"),sQuery(id+"F2.wireOp",EDGE,"E22.4.0.2")])]});
            var Q14;
            Q14=makeQuery(id+"F4.opExtrude","SWEPT_BODY",BODY,{"disambiguationData":[OSD([sQuery(id+"F2.wireOp",EDGE,"E22.3.0.9"),sQuery(id+"F2.wireOp",EDGE,"E22.3.0.10"),sQuery(id+"F2.wireOp",EDGE,"E22.3.0.11")])]});
            var Q15;
            Q15=makeQuery(id+"F4.opExtrude","SWEPT_BODY",BODY,{"disambiguationData":[OSD([sQuery(id+"F2.wireOp",EDGE,"E22.3.0.0"),sQuery(id+"F2.wireOp",EDGE,"E22.3.0.1"),sQuery(id+"F2.wireOp",EDGE,"E22.3.0.2")])]});
            var Q16;
            Q16=makeQuery(id+"F4.opExtrude","SWEPT_BODY",BODY,{"disambiguationData":[OSD([sQuery(id+"F2.wireOp",EDGE,"E22.2.0.9"),sQuery(id+"F2.wireOp",EDGE,"E22.2.0.10"),sQuery(id+"F2.wireOp",EDGE,"E22.2.0.11")])]});
            var Q17;
            Q17=makeQuery(id+"F4.opExtrude","SWEPT_BODY",BODY,{"disambiguationData":[OSD([sQuery(id+"F2.wireOp",EDGE,"E22.2.0.0"),sQuery(id+"F2.wireOp",EDGE,"E22.2.0.1"),sQuery(id+"F2.wireOp",EDGE,"E22.2.0.2")])]});
            var Q18;
            Q18=makeQuery(id+"F4.opExtrude","SWEPT_BODY",BODY,{"disambiguationData":[OSD([sQuery(id+"F2.wireOp",EDGE,"E22.1.0.9"),sQuery(id+"F2.wireOp",EDGE,"E22.1.0.10"),sQuery(id+"F2.wireOp",EDGE,"E22.1.0.11")])]});
            var Q19;
            Q19=makeQuery(id+"F4.opExtrude","SWEPT_BODY",BODY,{"disambiguationData":[OSD([sQuery(id+"F2.wireOp",EDGE,"E22.1.0.0"),sQuery(id+"F2.wireOp",EDGE,"E22.1.0.1"),sQuery(id+"F2.wireOp",EDGE,"E22.1.0.2")])]});
            var Q20;
            Q20=makeQuery(id+"F4.opExtrude","SWEPT_BODY",BODY,{"disambiguationData":[OSD([sQuery(id+"F2.wireOp",EDGE,"E21.27.10.0"),sQuery(id+"F2.wireOp",EDGE,"E21.30.10.0"),sQuery(id+"F2.wireOp",EDGE,"E21.33.10.0")])]});
            var Q21;
            Q21=makeQuery(id+"F4.opExtrude","SWEPT_BODY",BODY,{"disambiguationData":[OSD([sQuery(id+"F2.wireOp",EDGE,"E21.0.10.0"),sQuery(id+"F2.wireOp",EDGE,"E21.3.10.0"),sQuery(id+"F2.wireOp",EDGE,"E21.6.10.0")])]});
            var Q22;
            Q22=makeQuery(id+"F4.opExtrude","SWEPT_BODY",BODY,{"disambiguationData":[OSD([sQuery(id+"F2.wireOp",EDGE,"E20.27.9.0"),sQuery(id+"F2.wireOp",EDGE,"E20.30.9.0"),sQuery(id+"F2.wireOp",EDGE,"E20.33.9.0")])]});
            var Q23;
            Q23=makeQuery(id+"F4.opExtrude","SWEPT_BODY",BODY,{"disambiguationData":[OSD([sQuery(id+"F2.wireOp",EDGE,"E20.0.9.0"),sQuery(id+"F2.wireOp",EDGE,"E20.3.9.0"),sQuery(id+"F2.wireOp",EDGE,"E20.6.9.0")])]});
            var Q24;
            Q24=makeQuery(id+"F4.opExtrude","SWEPT_BODY",BODY,{"disambiguationData":[OSD([sQuery(id+"F2.wireOp",EDGE,"E20.27.8.0"),sQuery(id+"F2.wireOp",EDGE,"E20.30.8.0"),sQuery(id+"F2.wireOp",EDGE,"E20.33.8.0")])]});
            var Q25;
            Q25=makeQuery(id+"F4.opExtrude","SWEPT_BODY",BODY,{"disambiguationData":[OSD([sQuery(id+"F2.wireOp",EDGE,"E20.0.8.0"),sQuery(id+"F2.wireOp",EDGE,"E20.3.8.0"),sQuery(id+"F2.wireOp",EDGE,"E20.6.8.0")])]});
            var Q26;
            Q26=makeQuery(id+"F4.opExtrude","SWEPT_BODY",BODY,{"disambiguationData":[OSD([sQuery(id+"F2.wireOp",EDGE,"E20.27.7.0"),sQuery(id+"F2.wireOp",EDGE,"E20.30.7.0"),sQuery(id+"F2.wireOp",EDGE,"E20.33.7.0")])]});
            var Q27;
            Q27=makeQuery(id+"F4.opExtrude","SWEPT_BODY",BODY,{"disambiguationData":[OSD([sQuery(id+"F2.wireOp",EDGE,"E20.0.7.0"),sQuery(id+"F2.wireOp",EDGE,"E20.3.7.0"),sQuery(id+"F2.wireOp",EDGE,"E20.6.7.0")])]});
            var Q28;
            Q28=makeQuery(id+"F4.opExtrude","SWEPT_BODY",BODY,{"disambiguationData":[OSD([sQuery(id+"F2.wireOp",EDGE,"E20.27.6.0"),sQuery(id+"F2.wireOp",EDGE,"E20.30.6.0"),sQuery(id+"F2.wireOp",EDGE,"E20.33.6.0")])]});
            var Q29;
            Q29=makeQuery(id+"F4.opExtrude","SWEPT_BODY",BODY,{"disambiguationData":[OSD([sQuery(id+"F2.wireOp",EDGE,"E20.0.6.0"),sQuery(id+"F2.wireOp",EDGE,"E20.3.6.0"),sQuery(id+"F2.wireOp",EDGE,"E20.6.6.0")])]});
            var Q30;
            Q30=makeQuery(id+"F4.opExtrude","SWEPT_BODY",BODY,{"disambiguationData":[OSD([sQuery(id+"F2.wireOp",EDGE,"E20.27.5.0"),sQuery(id+"F2.wireOp",EDGE,"E20.30.5.0"),sQuery(id+"F2.wireOp",EDGE,"E20.33.5.0")])]});
            var Q31;
            Q31=makeQuery(id+"F4.opExtrude","SWEPT_BODY",BODY,{"disambiguationData":[OSD([sQuery(id+"F2.wireOp",EDGE,"E20.0.5.0"),sQuery(id+"F2.wireOp",EDGE,"E20.3.5.0"),sQuery(id+"F2.wireOp",EDGE,"E20.6.5.0")])]});
            var Q32;
            Q32=makeQuery(id+"F4.opExtrude","SWEPT_BODY",BODY,{"disambiguationData":[OSD([sQuery(id+"F2.wireOp",EDGE,"E19.27.4.0"),sQuery(id+"F2.wireOp",EDGE,"E19.30.4.0"),sQuery(id+"F2.wireOp",EDGE,"E19.33.4.0")])]});
            var Q33;
            Q33=makeQuery(id+"F4.opExtrude","SWEPT_BODY",BODY,{"disambiguationData":[OSD([sQuery(id+"F2.wireOp",EDGE,"E19.0.4.0"),sQuery(id+"F2.wireOp",EDGE,"E19.3.4.0"),sQuery(id+"F2.wireOp",EDGE,"E19.6.4.0")])]});
            var Q34;
            Q34=makeQuery(id+"F4.opExtrude","SWEPT_BODY",BODY,{"disambiguationData":[OSD([sQuery(id+"F2.wireOp",EDGE,"E19.27.3.0"),sQuery(id+"F2.wireOp",EDGE,"E19.30.3.0"),sQuery(id+"F2.wireOp",EDGE,"E19.33.3.0")])]});
            var Q35;
            Q35=makeQuery(id+"F4.opExtrude","SWEPT_BODY",BODY,{"disambiguationData":[OSD([sQuery(id+"F2.wireOp",EDGE,"E19.0.3.0"),sQuery(id+"F2.wireOp",EDGE,"E19.3.3.0"),sQuery(id+"F2.wireOp",EDGE,"E19.6.3.0")])]});
            var Q36;
            Q36=makeQuery(id+"F4.opExtrude","SWEPT_BODY",BODY,{"disambiguationData":[OSD([sQuery(id+"F2.wireOp",EDGE,"E18.2.0.9"),sQuery(id+"F2.wireOp",EDGE,"E18.2.0.10"),sQuery(id+"F2.wireOp",EDGE,"E18.2.0.11")])]});
            var Q37;
            Q37=makeQuery(id+"F4.opExtrude","SWEPT_BODY",BODY,{"disambiguationData":[OSD([sQuery(id+"F2.wireOp",EDGE,"E18.2.0.0"),sQuery(id+"F2.wireOp",EDGE,"E18.2.0.1"),sQuery(id+"F2.wireOp",EDGE,"E18.2.0.2")])]});
            var Q38;
            Q38=makeQuery(id+"F4.opExtrude","SWEPT_BODY",BODY,{"disambiguationData":[OSD([sQuery(id+"F2.wireOp",EDGE,"E18.1.0.9"),sQuery(id+"F2.wireOp",EDGE,"E18.1.0.10"),sQuery(id+"F2.wireOp",EDGE,"E18.1.0.11")])]});
            var Q39;
            Q39=makeQuery(id+"F4.opExtrude","SWEPT_BODY",BODY,{"disambiguationData":[OSD([sQuery(id+"F2.wireOp",EDGE,"E18.1.0.0"),sQuery(id+"F2.wireOp",EDGE,"E18.1.0.1"),sQuery(id+"F2.wireOp",EDGE,"E18.1.0.2")])]});
            var Q40;
            Q40=makeQuery(id+"F4.opExtrude","SWEPT_BODY",BODY,{"disambiguationData":[OSD([sQuery(id+"F2.wireOp",EDGE,"E5.3"),sQuery(id+"F2.wireOp",EDGE,"E9.0"),sQuery(id+"F2.wireOp",EDGE,"E11.trimOffspring")])]});
            var Q41;
            Q41=makeQuery(id+"F4.opExtrude","SWEPT_BODY",BODY,{"disambiguationData":[OSD([sQuery(id+"F2.wireOp",EDGE,"E5.1"),sQuery(id+"F2.wireOp",EDGE,"E6.0"),sQuery(id+"F2.wireOp",EDGE,"E10.trimOffspring")])]});
            var Q42;
            Q42=makeQuery(id+"F4.opExtrude","SWEPT_BODY",BODY,{"disambiguationData":[OSD([sQuery(id+"F2.wireOp",EDGE,"E5.2"),sQuery(id+"F2.wireOp",EDGE,"E7.0"),sQuery(id+"F2.wireOp",EDGE,"E13.trimOffspring")])]});
            var Q43;
            Q43=makeQuery(id+"F4.opExtrude","SWEPT_BODY",BODY,{"disambiguationData":[OSD([sQuery(id+"F2.wireOp",EDGE,"E21.9.10.0"),sQuery(id+"F2.wireOp",EDGE,"E21.12.10.0"),sQuery(id+"F2.wireOp",EDGE,"E21.15.10.0")])]});
            var Q44;
            Q44=makeQuery(id+"F4.opExtrude","SWEPT_BODY",BODY,{"disambiguationData":[OSD([sQuery(id+"F2.wireOp",EDGE,"E22.10.0.6"),sQuery(id+"F2.wireOp",EDGE,"E22.10.0.7"),sQuery(id+"F2.wireOp",EDGE,"E22.10.0.8")])]});
            var Q45;
            Q45=makeQuery(id+"F4.opExtrude","SWEPT_BODY",BODY,{"disambiguationData":[OSD([sQuery(id+"F2.wireOp",EDGE,"E22.10.0.3"),sQuery(id+"F2.wireOp",EDGE,"E22.10.0.4"),sQuery(id+"F2.wireOp",EDGE,"E22.10.0.5")])]});
            var Q46;
            Q46=makeQuery(id+"F4.opExtrude","SWEPT_BODY",BODY,{"disambiguationData":[OSD([sQuery(id+"F2.wireOp",EDGE,"E22.9.0.6"),sQuery(id+"F2.wireOp",EDGE,"E22.9.0.7"),sQuery(id+"F2.wireOp",EDGE,"E22.9.0.8")])]});
            var Q47;
            Q47=makeQuery(id+"F4.opExtrude","SWEPT_BODY",BODY,{"disambiguationData":[OSD([sQuery(id+"F2.wireOp",EDGE,"E22.9.0.3"),sQuery(id+"F2.wireOp",EDGE,"E22.9.0.4"),sQuery(id+"F2.wireOp",EDGE,"E22.9.0.5")])]});
            var Q48;
            Q48=makeQuery(id+"F4.opExtrude","SWEPT_BODY",BODY,{"disambiguationData":[OSD([sQuery(id+"F2.wireOp",EDGE,"E22.8.0.6"),sQuery(id+"F2.wireOp",EDGE,"E22.8.0.7"),sQuery(id+"F2.wireOp",EDGE,"E22.8.0.8")])]});
            var Q49;
            Q49=makeQuery(id+"F4.opExtrude","SWEPT_BODY",BODY,{"disambiguationData":[OSD([sQuery(id+"F2.wireOp",EDGE,"E22.8.0.3"),sQuery(id+"F2.wireOp",EDGE,"E22.8.0.4"),sQuery(id+"F2.wireOp",EDGE,"E22.8.0.5")])]});
            var Q50;
            Q50=makeQuery(id+"F4.opExtrude","SWEPT_BODY",BODY,{"disambiguationData":[OSD([sQuery(id+"F2.wireOp",EDGE,"E22.7.0.6"),sQuery(id+"F2.wireOp",EDGE,"E22.7.0.7"),sQuery(id+"F2.wireOp",EDGE,"E22.7.0.8")])]});
            var Q51;
            Q51=makeQuery(id+"F4.opExtrude","SWEPT_BODY",BODY,{"disambiguationData":[OSD([sQuery(id+"F2.wireOp",EDGE,"E22.7.0.3"),sQuery(id+"F2.wireOp",EDGE,"E22.7.0.4"),sQuery(id+"F2.wireOp",EDGE,"E22.7.0.5")])]});
            var Q52;
            Q52=makeQuery(id+"F4.opExtrude","SWEPT_BODY",BODY,{"disambiguationData":[OSD([sQuery(id+"F2.wireOp",EDGE,"E22.6.0.6"),sQuery(id+"F2.wireOp",EDGE,"E22.6.0.7"),sQuery(id+"F2.wireOp",EDGE,"E22.6.0.8")])]});
            var Q53;
            Q53=makeQuery(id+"F4.opExtrude","SWEPT_BODY",BODY,{"disambiguationData":[OSD([sQuery(id+"F2.wireOp",EDGE,"E22.6.0.3"),sQuery(id+"F2.wireOp",EDGE,"E22.6.0.4"),sQuery(id+"F2.wireOp",EDGE,"E22.6.0.5")])]});
            var Q54;
            Q54=makeQuery(id+"F4.opExtrude","SWEPT_BODY",BODY,{"disambiguationData":[OSD([sQuery(id+"F2.wireOp",EDGE,"E22.5.0.6"),sQuery(id+"F2.wireOp",EDGE,"E22.5.0.7"),sQuery(id+"F2.wireOp",EDGE,"E22.5.0.8")])]});
            var Q55;
            Q55=makeQuery(id+"F4.opExtrude","SWEPT_BODY",BODY,{"disambiguationData":[OSD([sQuery(id+"F2.wireOp",EDGE,"E22.5.0.3"),sQuery(id+"F2.wireOp",EDGE,"E22.5.0.4"),sQuery(id+"F2.wireOp",EDGE,"E22.5.0.5")])]});
            var Q56;
            Q56=makeQuery(id+"F4.opExtrude","SWEPT_BODY",BODY,{"disambiguationData":[OSD([sQuery(id+"F2.wireOp",EDGE,"E22.4.0.6"),sQuery(id+"F2.wireOp",EDGE,"E22.4.0.7"),sQuery(id+"F2.wireOp",EDGE,"E22.4.0.8")])]});
            var Q57;
            Q57=makeQuery(id+"F4.opExtrude","SWEPT_BODY",BODY,{"disambiguationData":[OSD([sQuery(id+"F2.wireOp",EDGE,"E22.4.0.3"),sQuery(id+"F2.wireOp",EDGE,"E22.4.0.4"),sQuery(id+"F2.wireOp",EDGE,"E22.4.0.5")])]});
            var Q58;
            Q58=makeQuery(id+"F4.opExtrude","SWEPT_BODY",BODY,{"disambiguationData":[OSD([sQuery(id+"F2.wireOp",EDGE,"E22.3.0.6"),sQuery(id+"F2.wireOp",EDGE,"E22.3.0.7"),sQuery(id+"F2.wireOp",EDGE,"E22.3.0.8")])]});
            var Q59;
            Q59=makeQuery(id+"F4.opExtrude","SWEPT_BODY",BODY,{"disambiguationData":[OSD([sQuery(id+"F2.wireOp",EDGE,"E22.3.0.3"),sQuery(id+"F2.wireOp",EDGE,"E22.3.0.4"),sQuery(id+"F2.wireOp",EDGE,"E22.3.0.5")])]});
            var Q60;
            Q60=makeQuery(id+"F4.opExtrude","SWEPT_BODY",BODY,{"disambiguationData":[OSD([sQuery(id+"F2.wireOp",EDGE,"E22.2.0.6"),sQuery(id+"F2.wireOp",EDGE,"E22.2.0.7"),sQuery(id+"F2.wireOp",EDGE,"E22.2.0.8")])]});
            var Q61;
            Q61=makeQuery(id+"F4.opExtrude","SWEPT_BODY",BODY,{"disambiguationData":[OSD([sQuery(id+"F2.wireOp",EDGE,"E22.2.0.3"),sQuery(id+"F2.wireOp",EDGE,"E22.2.0.4"),sQuery(id+"F2.wireOp",EDGE,"E22.2.0.5")])]});
            var Q62;
            Q62=makeQuery(id+"F4.opExtrude","SWEPT_BODY",BODY,{"disambiguationData":[OSD([sQuery(id+"F2.wireOp",EDGE,"E22.1.0.6"),sQuery(id+"F2.wireOp",EDGE,"E22.1.0.7"),sQuery(id+"F2.wireOp",EDGE,"E22.1.0.8")])]});
            var Q63;
            Q63=makeQuery(id+"F4.opExtrude","SWEPT_BODY",BODY,{"disambiguationData":[OSD([sQuery(id+"F2.wireOp",EDGE,"E22.1.0.3"),sQuery(id+"F2.wireOp",EDGE,"E22.1.0.4"),sQuery(id+"F2.wireOp",EDGE,"E22.1.0.5")])]});
            var Q64;
            Q64=makeQuery(id+"F4.opExtrude","SWEPT_BODY",BODY,{"disambiguationData":[OSD([sQuery(id+"F2.wireOp",EDGE,"E21.18.10.0"),sQuery(id+"F2.wireOp",EDGE,"E21.21.10.0"),sQuery(id+"F2.wireOp",EDGE,"E21.24.10.0")])]});
            var Q65;
            Q65=makeQuery(id+"F4.opExtrude","SWEPT_BODY",BODY,{"disambiguationData":[OSD([sQuery(id+"F2.wireOp",EDGE,"E20.18.9.0"),sQuery(id+"F2.wireOp",EDGE,"E20.21.9.0"),sQuery(id+"F2.wireOp",EDGE,"E20.24.9.0")])]});
            var Q66;
            Q66=makeQuery(id+"F4.opExtrude","SWEPT_BODY",BODY,{"disambiguationData":[OSD([sQuery(id+"F2.wireOp",EDGE,"E20.9.9.0"),sQuery(id+"F2.wireOp",EDGE,"E20.12.9.0"),sQuery(id+"F2.wireOp",EDGE,"E20.15.9.0")])]});
            var Q67;
            Q67=makeQuery(id+"F4.opExtrude","SWEPT_BODY",BODY,{"disambiguationData":[OSD([sQuery(id+"F2.wireOp",EDGE,"E20.18.8.0"),sQuery(id+"F2.wireOp",EDGE,"E20.21.8.0"),sQuery(id+"F2.wireOp",EDGE,"E20.24.8.0")])]});
            var Q68;
            Q68=makeQuery(id+"F4.opExtrude","SWEPT_BODY",BODY,{"disambiguationData":[OSD([sQuery(id+"F2.wireOp",EDGE,"E20.9.8.0"),sQuery(id+"F2.wireOp",EDGE,"E20.12.8.0"),sQuery(id+"F2.wireOp",EDGE,"E20.15.8.0")])]});
            var Q69;
            Q69=makeQuery(id+"F4.opExtrude","SWEPT_BODY",BODY,{"disambiguationData":[OSD([sQuery(id+"F2.wireOp",EDGE,"E20.18.7.0"),sQuery(id+"F2.wireOp",EDGE,"E20.21.7.0"),sQuery(id+"F2.wireOp",EDGE,"E20.24.7.0")])]});
            var Q70;
            Q70=makeQuery(id+"F4.opExtrude","SWEPT_BODY",BODY,{"disambiguationData":[OSD([sQuery(id+"F2.wireOp",EDGE,"E20.9.7.0"),sQuery(id+"F2.wireOp",EDGE,"E20.12.7.0"),sQuery(id+"F2.wireOp",EDGE,"E20.15.7.0")])]});
            var Q71;
            Q71=makeQuery(id+"F4.opExtrude","SWEPT_BODY",BODY,{"disambiguationData":[OSD([sQuery(id+"F2.wireOp",EDGE,"E20.18.6.0"),sQuery(id+"F2.wireOp",EDGE,"E20.21.6.0"),sQuery(id+"F2.wireOp",EDGE,"E20.24.6.0")])]});
            var Q72;
            Q72=makeQuery(id+"F4.opExtrude","SWEPT_BODY",BODY,{"disambiguationData":[OSD([sQuery(id+"F2.wireOp",EDGE,"E20.9.6.0"),sQuery(id+"F2.wireOp",EDGE,"E20.12.6.0"),sQuery(id+"F2.wireOp",EDGE,"E20.15.6.0")])]});
            var Q73;
            Q73=makeQuery(id+"F4.opExtrude","SWEPT_BODY",BODY,{"disambiguationData":[OSD([sQuery(id+"F2.wireOp",EDGE,"E20.18.5.0"),sQuery(id+"F2.wireOp",EDGE,"E20.21.5.0"),sQuery(id+"F2.wireOp",EDGE,"E20.24.5.0")])]});
            var Q74;
            Q74=makeQuery(id+"F4.opExtrude","SWEPT_BODY",BODY,{"disambiguationData":[OSD([sQuery(id+"F2.wireOp",EDGE,"E20.9.5.0"),sQuery(id+"F2.wireOp",EDGE,"E20.12.5.0"),sQuery(id+"F2.wireOp",EDGE,"E20.15.5.0")])]});
            var Q75;
            Q75=makeQuery(id+"F4.opExtrude","SWEPT_BODY",BODY,{"disambiguationData":[OSD([sQuery(id+"F2.wireOp",EDGE,"E19.18.4.0"),sQuery(id+"F2.wireOp",EDGE,"E19.21.4.0"),sQuery(id+"F2.wireOp",EDGE,"E19.24.4.0")])]});
            var Q76;
            Q76=makeQuery(id+"F4.opExtrude","SWEPT_BODY",BODY,{"disambiguationData":[OSD([sQuery(id+"F2.wireOp",EDGE,"E19.9.4.0"),sQuery(id+"F2.wireOp",EDGE,"E19.12.4.0"),sQuery(id+"F2.wireOp",EDGE,"E19.15.4.0")])]});
            var Q77;
            Q77=makeQuery(id+"F4.opExtrude","SWEPT_BODY",BODY,{"disambiguationData":[OSD([sQuery(id+"F2.wireOp",EDGE,"E19.18.3.0"),sQuery(id+"F2.wireOp",EDGE,"E19.21.3.0"),sQuery(id+"F2.wireOp",EDGE,"E19.24.3.0")])]});
            var Q78;
            Q78=makeQuery(id+"F4.opExtrude","SWEPT_BODY",BODY,{"disambiguationData":[OSD([sQuery(id+"F2.wireOp",EDGE,"E19.9.3.0"),sQuery(id+"F2.wireOp",EDGE,"E19.12.3.0"),sQuery(id+"F2.wireOp",EDGE,"E19.15.3.0")])]});
            var Q79;
            Q79=makeQuery(id+"F4.opExtrude","SWEPT_BODY",BODY,{"disambiguationData":[OSD([sQuery(id+"F2.wireOp",EDGE,"E18.2.0.6"),sQuery(id+"F2.wireOp",EDGE,"E18.2.0.7"),sQuery(id+"F2.wireOp",EDGE,"E18.2.0.8")])]});
            var Q80;
            Q80=makeQuery(id+"F4.opExtrude","SWEPT_BODY",BODY,{"disambiguationData":[OSD([sQuery(id+"F2.wireOp",EDGE,"E18.2.0.3"),sQuery(id+"F2.wireOp",EDGE,"E18.2.0.4"),sQuery(id+"F2.wireOp",EDGE,"E18.2.0.5")])]});
            var Q81;
            Q81=makeQuery(id+"F4.opExtrude","SWEPT_BODY",BODY,{"disambiguationData":[OSD([sQuery(id+"F2.wireOp",EDGE,"E18.1.0.6"),sQuery(id+"F2.wireOp",EDGE,"E18.1.0.7"),sQuery(id+"F2.wireOp",EDGE,"E18.1.0.8")])]});
            var Q82;
            Q82=makeQuery(id+"F4.opExtrude","SWEPT_BODY",BODY,{"disambiguationData":[OSD([sQuery(id+"F2.wireOp",EDGE,"E18.1.0.3"),sQuery(id+"F2.wireOp",EDGE,"E18.1.0.4"),sQuery(id+"F2.wireOp",EDGE,"E18.1.0.5")])]});
            var Q83;
            Q83=makeQuery(id+"F4.opExtrude","SWEPT_BODY",BODY,{"disambiguationData":[OSD([sQuery(id+"F2.wireOp",EDGE,"E5.5"),sQuery(id+"F2.wireOp",EDGE,"E12.trimOffspring"),sQuery(id+"F2.wireOp",EDGE,"E16.trimOffspring")])]});
            var Q84;
            Q84=makeQuery(id+"F4.opExtrude","SWEPT_BODY",BODY,{"disambiguationData":[OSD([sQuery(id+"F2.wireOp",EDGE,"E5.4"),sQuery(id+"F2.wireOp",EDGE,"E15.trimOffspring"),sQuery(id+"F2.wireOp",EDGE,"E17.trimOffspring")])]});
            var Q85;
            Q85=makeQuery(id+"F4.opExtrude","SWEPT_BODY",BODY,{"disambiguationData":[OSD([sQuery(id+"F2.wireOp",EDGE,"E5.0"),sQuery(id+"F2.wireOp",EDGE,"E8.0"),sQuery(id+"F2.wireOp",EDGE,"E14.trimOffspring")])]});
            var Q86;
            Q86=makeQuery(id+"F1.opExtrude","SWEPT_EDGE",EDGE,{"disambiguationData":[OSD([sQuery(id+"F0.wireOp",EDGE,"E0.bottom"),sQuery(id+"F0.wireOp",EDGE,"E0.right")])]});
            var Q87;
            Q87=makeQuery(id+"F1.opExtrude","SWEPT_EDGE",EDGE,{"disambiguationData":[OSD([sQuery(id+"F0.wireOp",EDGE,"E0.bottom"),sQuery(id+"F0.wireOp",EDGE,"E0.right")])]});
            transform(context, id + "F5", {"entities" : qUnion([Q0, Q1, Q2, Q3, Q4, Q5, Q6, Q7, Q8, Q9, Q10, Q11, Q12, Q13, Q14, Q15, Q16, Q17, Q18, Q19, Q20, Q21, Q22, Q23, Q24, Q25, Q26, Q27, Q28, Q29, Q30, Q31, Q32, Q33, Q34, Q35, Q36, Q37, Q38, Q39, Q40, Q41, Q42, Q43, Q44, Q45, Q46, Q47, Q48, Q49, Q50, Q51, Q52, Q53, Q54, Q55, Q56, Q57, Q58, Q59, Q60, Q61, Q62, Q63, Q64, Q65, Q66, Q67, Q68, Q69, Q70, Q71, Q72, Q73, Q74, Q75, Q76, Q77, Q78, Q79, Q80, Q81, Q82, Q83, Q84, Q85]), "transformType" : TransformType.ROTATION, "transformAxis" : qUnion([Q87]), "angle" : 90 * degree, "oppositeDirection" : true, "makeCopy" : false});
        }
        {
            var Q0;
            Q0=makeQuery(id+"F4.opExtrude","SWEPT_BODY",BODY,{"disambiguationData":[OSD([sQuery(id+"F2.wireOp",EDGE,"E22.10.0.9"),sQuery(id+"F2.wireOp",EDGE,"E22.10.0.10"),sQuery(id+"F2.wireOp",EDGE,"E22.10.0.11")])]});
            var Q1;
            Q1=makeQuery(id+"F4.opExtrude","SWEPT_BODY",BODY,{"disambiguationData":[OSD([sQuery(id+"F2.wireOp",EDGE,"E22.10.0.6"),sQuery(id+"F2.wireOp",EDGE,"E22.10.0.7"),sQuery(id+"F2.wireOp",EDGE,"E22.10.0.8")])]});
            var Q2;
            Q2=makeQuery(id+"F4.opExtrude","SWEPT_BODY",BODY,{"disambiguationData":[OSD([sQuery(id+"F2.wireOp",EDGE,"E22.10.0.3"),sQuery(id+"F2.wireOp",EDGE,"E22.10.0.4"),sQuery(id+"F2.wireOp",EDGE,"E22.10.0.5")])]});
            var Q3;
            Q3=makeQuery(id+"F4.opExtrude","SWEPT_BODY",BODY,{"disambiguationData":[OSD([sQuery(id+"F2.wireOp",EDGE,"E22.10.0.0"),sQuery(id+"F2.wireOp",EDGE,"E22.10.0.1"),sQuery(id+"F2.wireOp",EDGE,"E22.10.0.2")])]});
            var Q4;
            Q4=makeQuery(id+"F4.opExtrude","SWEPT_BODY",BODY,{"disambiguationData":[OSD([sQuery(id+"F2.wireOp",EDGE,"E22.9.0.9"),sQuery(id+"F2.wireOp",EDGE,"E22.9.0.10"),sQuery(id+"F2.wireOp",EDGE,"E22.9.0.11")])]});
            var Q5;
            Q5=makeQuery(id+"F4.opExtrude","SWEPT_BODY",BODY,{"disambiguationData":[OSD([sQuery(id+"F2.wireOp",EDGE,"E22.9.0.6"),sQuery(id+"F2.wireOp",EDGE,"E22.9.0.7"),sQuery(id+"F2.wireOp",EDGE,"E22.9.0.8")])]});
            var Q6;
            Q6=makeQuery(id+"F4.opExtrude","SWEPT_BODY",BODY,{"disambiguationData":[OSD([sQuery(id+"F2.wireOp",EDGE,"E22.9.0.3"),sQuery(id+"F2.wireOp",EDGE,"E22.9.0.4"),sQuery(id+"F2.wireOp",EDGE,"E22.9.0.5")])]});
            var Q7;
            Q7=makeQuery(id+"F4.opExtrude","SWEPT_BODY",BODY,{"disambiguationData":[OSD([sQuery(id+"F2.wireOp",EDGE,"E22.9.0.0"),sQuery(id+"F2.wireOp",EDGE,"E22.9.0.1"),sQuery(id+"F2.wireOp",EDGE,"E22.9.0.2")])]});
            var Q8;
            Q8=makeQuery(id+"F4.opExtrude","SWEPT_BODY",BODY,{"disambiguationData":[OSD([sQuery(id+"F2.wireOp",EDGE,"E22.8.0.9"),sQuery(id+"F2.wireOp",EDGE,"E22.8.0.10"),sQuery(id+"F2.wireOp",EDGE,"E22.8.0.11")])]});
            var Q9;
            Q9=makeQuery(id+"F4.opExtrude","SWEPT_BODY",BODY,{"disambiguationData":[OSD([sQuery(id+"F2.wireOp",EDGE,"E22.8.0.6"),sQuery(id+"F2.wireOp",EDGE,"E22.8.0.7"),sQuery(id+"F2.wireOp",EDGE,"E22.8.0.8")])]});
            var Q10;
            Q10=makeQuery(id+"F4.opExtrude","SWEPT_BODY",BODY,{"disambiguationData":[OSD([sQuery(id+"F2.wireOp",EDGE,"E22.8.0.3"),sQuery(id+"F2.wireOp",EDGE,"E22.8.0.4"),sQuery(id+"F2.wireOp",EDGE,"E22.8.0.5")])]});
            var Q11;
            Q11=makeQuery(id+"F4.opExtrude","SWEPT_BODY",BODY,{"disambiguationData":[OSD([sQuery(id+"F2.wireOp",EDGE,"E22.8.0.0"),sQuery(id+"F2.wireOp",EDGE,"E22.8.0.1"),sQuery(id+"F2.wireOp",EDGE,"E22.8.0.2")])]});
            var Q12;
            Q12=makeQuery(id+"F4.opExtrude","SWEPT_BODY",BODY,{"disambiguationData":[OSD([sQuery(id+"F2.wireOp",EDGE,"E22.7.0.9"),sQuery(id+"F2.wireOp",EDGE,"E22.7.0.10"),sQuery(id+"F2.wireOp",EDGE,"E22.7.0.11")])]});
            var Q13;
            Q13=makeQuery(id+"F4.opExtrude","SWEPT_BODY",BODY,{"disambiguationData":[OSD([sQuery(id+"F2.wireOp",EDGE,"E22.7.0.6"),sQuery(id+"F2.wireOp",EDGE,"E22.7.0.7"),sQuery(id+"F2.wireOp",EDGE,"E22.7.0.8")])]});
            var Q14;
            Q14=makeQuery(id+"F4.opExtrude","SWEPT_BODY",BODY,{"disambiguationData":[OSD([sQuery(id+"F2.wireOp",EDGE,"E22.7.0.3"),sQuery(id+"F2.wireOp",EDGE,"E22.7.0.4"),sQuery(id+"F2.wireOp",EDGE,"E22.7.0.5")])]});
            var Q15;
            Q15=makeQuery(id+"F4.opExtrude","SWEPT_BODY",BODY,{"disambiguationData":[OSD([sQuery(id+"F2.wireOp",EDGE,"E22.7.0.0"),sQuery(id+"F2.wireOp",EDGE,"E22.7.0.1"),sQuery(id+"F2.wireOp",EDGE,"E22.7.0.2")])]});
            var Q16;
            Q16=makeQuery(id+"F4.opExtrude","SWEPT_BODY",BODY,{"disambiguationData":[OSD([sQuery(id+"F2.wireOp",EDGE,"E22.6.0.9"),sQuery(id+"F2.wireOp",EDGE,"E22.6.0.10"),sQuery(id+"F2.wireOp",EDGE,"E22.6.0.11")])]});
            var Q17;
            Q17=makeQuery(id+"F4.opExtrude","SWEPT_BODY",BODY,{"disambiguationData":[OSD([sQuery(id+"F2.wireOp",EDGE,"E22.6.0.6"),sQuery(id+"F2.wireOp",EDGE,"E22.6.0.7"),sQuery(id+"F2.wireOp",EDGE,"E22.6.0.8")])]});
            var Q18;
            Q18=makeQuery(id+"F4.opExtrude","SWEPT_BODY",BODY,{"disambiguationData":[OSD([sQuery(id+"F2.wireOp",EDGE,"E22.6.0.3"),sQuery(id+"F2.wireOp",EDGE,"E22.6.0.4"),sQuery(id+"F2.wireOp",EDGE,"E22.6.0.5")])]});
            var Q19;
            Q19=makeQuery(id+"F4.opExtrude","SWEPT_BODY",BODY,{"disambiguationData":[OSD([sQuery(id+"F2.wireOp",EDGE,"E22.6.0.0"),sQuery(id+"F2.wireOp",EDGE,"E22.6.0.1"),sQuery(id+"F2.wireOp",EDGE,"E22.6.0.2")])]});
            var Q20;
            Q20=makeQuery(id+"F4.opExtrude","SWEPT_BODY",BODY,{"disambiguationData":[OSD([sQuery(id+"F2.wireOp",EDGE,"E22.5.0.9"),sQuery(id+"F2.wireOp",EDGE,"E22.5.0.10"),sQuery(id+"F2.wireOp",EDGE,"E22.5.0.11")])]});
            var Q21;
            Q21=makeQuery(id+"F4.opExtrude","SWEPT_BODY",BODY,{"disambiguationData":[OSD([sQuery(id+"F2.wireOp",EDGE,"E22.5.0.6"),sQuery(id+"F2.wireOp",EDGE,"E22.5.0.7"),sQuery(id+"F2.wireOp",EDGE,"E22.5.0.8")])]});
            var Q22;
            Q22=makeQuery(id+"F4.opExtrude","SWEPT_BODY",BODY,{"disambiguationData":[OSD([sQuery(id+"F2.wireOp",EDGE,"E22.5.0.3"),sQuery(id+"F2.wireOp",EDGE,"E22.5.0.4"),sQuery(id+"F2.wireOp",EDGE,"E22.5.0.5")])]});
            var Q23;
            Q23=makeQuery(id+"F4.opExtrude","SWEPT_BODY",BODY,{"disambiguationData":[OSD([sQuery(id+"F2.wireOp",EDGE,"E22.5.0.0"),sQuery(id+"F2.wireOp",EDGE,"E22.5.0.1"),sQuery(id+"F2.wireOp",EDGE,"E22.5.0.2")])]});
            var Q24;
            Q24=makeQuery(id+"F4.opExtrude","SWEPT_BODY",BODY,{"disambiguationData":[OSD([sQuery(id+"F2.wireOp",EDGE,"E22.4.0.9"),sQuery(id+"F2.wireOp",EDGE,"E22.4.0.10"),sQuery(id+"F2.wireOp",EDGE,"E22.4.0.11")])]});
            var Q25;
            Q25=makeQuery(id+"F4.opExtrude","SWEPT_BODY",BODY,{"disambiguationData":[OSD([sQuery(id+"F2.wireOp",EDGE,"E22.4.0.6"),sQuery(id+"F2.wireOp",EDGE,"E22.4.0.7"),sQuery(id+"F2.wireOp",EDGE,"E22.4.0.8")])]});
            var Q26;
            Q26=makeQuery(id+"F4.opExtrude","SWEPT_BODY",BODY,{"disambiguationData":[OSD([sQuery(id+"F2.wireOp",EDGE,"E22.4.0.3"),sQuery(id+"F2.wireOp",EDGE,"E22.4.0.4"),sQuery(id+"F2.wireOp",EDGE,"E22.4.0.5")])]});
            var Q27;
            Q27=makeQuery(id+"F4.opExtrude","SWEPT_BODY",BODY,{"disambiguationData":[OSD([sQuery(id+"F2.wireOp",EDGE,"E22.4.0.0"),sQuery(id+"F2.wireOp",EDGE,"E22.4.0.1"),sQuery(id+"F2.wireOp",EDGE,"E22.4.0.2")])]});
            var Q28;
            Q28=makeQuery(id+"F4.opExtrude","SWEPT_BODY",BODY,{"disambiguationData":[OSD([sQuery(id+"F2.wireOp",EDGE,"E22.3.0.9"),sQuery(id+"F2.wireOp",EDGE,"E22.3.0.10"),sQuery(id+"F2.wireOp",EDGE,"E22.3.0.11")])]});
            var Q29;
            Q29=makeQuery(id+"F4.opExtrude","SWEPT_BODY",BODY,{"disambiguationData":[OSD([sQuery(id+"F2.wireOp",EDGE,"E22.3.0.6"),sQuery(id+"F2.wireOp",EDGE,"E22.3.0.7"),sQuery(id+"F2.wireOp",EDGE,"E22.3.0.8")])]});
            var Q30;
            Q30=makeQuery(id+"F4.opExtrude","SWEPT_BODY",BODY,{"disambiguationData":[OSD([sQuery(id+"F2.wireOp",EDGE,"E22.3.0.3"),sQuery(id+"F2.wireOp",EDGE,"E22.3.0.4"),sQuery(id+"F2.wireOp",EDGE,"E22.3.0.5")])]});
            var Q31;
            Q31=makeQuery(id+"F4.opExtrude","SWEPT_BODY",BODY,{"disambiguationData":[OSD([sQuery(id+"F2.wireOp",EDGE,"E22.3.0.0"),sQuery(id+"F2.wireOp",EDGE,"E22.3.0.1"),sQuery(id+"F2.wireOp",EDGE,"E22.3.0.2")])]});
            var Q32;
            Q32=makeQuery(id+"F4.opExtrude","SWEPT_BODY",BODY,{"disambiguationData":[OSD([sQuery(id+"F2.wireOp",EDGE,"E22.2.0.9"),sQuery(id+"F2.wireOp",EDGE,"E22.2.0.10"),sQuery(id+"F2.wireOp",EDGE,"E22.2.0.11")])]});
            var Q33;
            Q33=makeQuery(id+"F4.opExtrude","SWEPT_BODY",BODY,{"disambiguationData":[OSD([sQuery(id+"F2.wireOp",EDGE,"E22.2.0.6"),sQuery(id+"F2.wireOp",EDGE,"E22.2.0.7"),sQuery(id+"F2.wireOp",EDGE,"E22.2.0.8")])]});
            var Q34;
            Q34=makeQuery(id+"F4.opExtrude","SWEPT_BODY",BODY,{"disambiguationData":[OSD([sQuery(id+"F2.wireOp",EDGE,"E22.2.0.3"),sQuery(id+"F2.wireOp",EDGE,"E22.2.0.4"),sQuery(id+"F2.wireOp",EDGE,"E22.2.0.5")])]});
            var Q35;
            Q35=makeQuery(id+"F4.opExtrude","SWEPT_BODY",BODY,{"disambiguationData":[OSD([sQuery(id+"F2.wireOp",EDGE,"E22.2.0.0"),sQuery(id+"F2.wireOp",EDGE,"E22.2.0.1"),sQuery(id+"F2.wireOp",EDGE,"E22.2.0.2")])]});
            var Q36;
            Q36=makeQuery(id+"F4.opExtrude","SWEPT_BODY",BODY,{"disambiguationData":[OSD([sQuery(id+"F2.wireOp",EDGE,"E22.1.0.9"),sQuery(id+"F2.wireOp",EDGE,"E22.1.0.10"),sQuery(id+"F2.wireOp",EDGE,"E22.1.0.11")])]});
            var Q37;
            Q37=makeQuery(id+"F4.opExtrude","SWEPT_BODY",BODY,{"disambiguationData":[OSD([sQuery(id+"F2.wireOp",EDGE,"E22.1.0.6"),sQuery(id+"F2.wireOp",EDGE,"E22.1.0.7"),sQuery(id+"F2.wireOp",EDGE,"E22.1.0.8")])]});
            var Q38;
            Q38=makeQuery(id+"F4.opExtrude","SWEPT_BODY",BODY,{"disambiguationData":[OSD([sQuery(id+"F2.wireOp",EDGE,"E22.1.0.3"),sQuery(id+"F2.wireOp",EDGE,"E22.1.0.4"),sQuery(id+"F2.wireOp",EDGE,"E22.1.0.5")])]});
            var Q39;
            Q39=makeQuery(id+"F4.opExtrude","SWEPT_BODY",BODY,{"disambiguationData":[OSD([sQuery(id+"F2.wireOp",EDGE,"E22.1.0.0"),sQuery(id+"F2.wireOp",EDGE,"E22.1.0.1"),sQuery(id+"F2.wireOp",EDGE,"E22.1.0.2")])]});
            var Q40;
            Q40=makeQuery(id+"F4.opExtrude","SWEPT_BODY",BODY,{"disambiguationData":[OSD([sQuery(id+"F2.wireOp",EDGE,"E21.27.10.0"),sQuery(id+"F2.wireOp",EDGE,"E21.30.10.0"),sQuery(id+"F2.wireOp",EDGE,"E21.33.10.0")])]});
            var Q41;
            Q41=makeQuery(id+"F4.opExtrude","SWEPT_BODY",BODY,{"disambiguationData":[OSD([sQuery(id+"F2.wireOp",EDGE,"E21.18.10.0"),sQuery(id+"F2.wireOp",EDGE,"E21.21.10.0"),sQuery(id+"F2.wireOp",EDGE,"E21.24.10.0")])]});
            var Q42;
            Q42=makeQuery(id+"F4.opExtrude","SWEPT_BODY",BODY,{"disambiguationData":[OSD([sQuery(id+"F2.wireOp",EDGE,"E21.9.10.0"),sQuery(id+"F2.wireOp",EDGE,"E21.12.10.0"),sQuery(id+"F2.wireOp",EDGE,"E21.15.10.0")])]});
            var Q43;
            Q43=makeQuery(id+"F4.opExtrude","SWEPT_BODY",BODY,{"disambiguationData":[OSD([sQuery(id+"F2.wireOp",EDGE,"E21.0.10.0"),sQuery(id+"F2.wireOp",EDGE,"E21.3.10.0"),sQuery(id+"F2.wireOp",EDGE,"E21.6.10.0")])]});
            var Q44;
            Q44=makeQuery(id+"F4.opExtrude","SWEPT_BODY",BODY,{"disambiguationData":[OSD([sQuery(id+"F2.wireOp",EDGE,"E20.27.9.0"),sQuery(id+"F2.wireOp",EDGE,"E20.30.9.0"),sQuery(id+"F2.wireOp",EDGE,"E20.33.9.0")])]});
            var Q45;
            Q45=makeQuery(id+"F4.opExtrude","SWEPT_BODY",BODY,{"disambiguationData":[OSD([sQuery(id+"F2.wireOp",EDGE,"E20.18.9.0"),sQuery(id+"F2.wireOp",EDGE,"E20.21.9.0"),sQuery(id+"F2.wireOp",EDGE,"E20.24.9.0")])]});
            var Q46;
            Q46=makeQuery(id+"F4.opExtrude","SWEPT_BODY",BODY,{"disambiguationData":[OSD([sQuery(id+"F2.wireOp",EDGE,"E20.9.9.0"),sQuery(id+"F2.wireOp",EDGE,"E20.12.9.0"),sQuery(id+"F2.wireOp",EDGE,"E20.15.9.0")])]});
            var Q47;
            Q47=makeQuery(id+"F4.opExtrude","SWEPT_BODY",BODY,{"disambiguationData":[OSD([sQuery(id+"F2.wireOp",EDGE,"E20.0.9.0"),sQuery(id+"F2.wireOp",EDGE,"E20.3.9.0"),sQuery(id+"F2.wireOp",EDGE,"E20.6.9.0")])]});
            var Q48;
            Q48=makeQuery(id+"F4.opExtrude","SWEPT_BODY",BODY,{"disambiguationData":[OSD([sQuery(id+"F2.wireOp",EDGE,"E20.27.8.0"),sQuery(id+"F2.wireOp",EDGE,"E20.30.8.0"),sQuery(id+"F2.wireOp",EDGE,"E20.33.8.0")])]});
            var Q49;
            Q49=makeQuery(id+"F4.opExtrude","SWEPT_BODY",BODY,{"disambiguationData":[OSD([sQuery(id+"F2.wireOp",EDGE,"E20.18.8.0"),sQuery(id+"F2.wireOp",EDGE,"E20.21.8.0"),sQuery(id+"F2.wireOp",EDGE,"E20.24.8.0")])]});
            var Q50;
            Q50=makeQuery(id+"F4.opExtrude","SWEPT_BODY",BODY,{"disambiguationData":[OSD([sQuery(id+"F2.wireOp",EDGE,"E20.9.8.0"),sQuery(id+"F2.wireOp",EDGE,"E20.12.8.0"),sQuery(id+"F2.wireOp",EDGE,"E20.15.8.0")])]});
            var Q51;
            Q51=makeQuery(id+"F4.opExtrude","SWEPT_BODY",BODY,{"disambiguationData":[OSD([sQuery(id+"F2.wireOp",EDGE,"E20.0.8.0"),sQuery(id+"F2.wireOp",EDGE,"E20.3.8.0"),sQuery(id+"F2.wireOp",EDGE,"E20.6.8.0")])]});
            var Q52;
            Q52=makeQuery(id+"F4.opExtrude","SWEPT_BODY",BODY,{"disambiguationData":[OSD([sQuery(id+"F2.wireOp",EDGE,"E20.27.7.0"),sQuery(id+"F2.wireOp",EDGE,"E20.30.7.0"),sQuery(id+"F2.wireOp",EDGE,"E20.33.7.0")])]});
            var Q53;
            Q53=makeQuery(id+"F4.opExtrude","SWEPT_BODY",BODY,{"disambiguationData":[OSD([sQuery(id+"F2.wireOp",EDGE,"E20.18.7.0"),sQuery(id+"F2.wireOp",EDGE,"E20.21.7.0"),sQuery(id+"F2.wireOp",EDGE,"E20.24.7.0")])]});
            var Q54;
            Q54=makeQuery(id+"F4.opExtrude","SWEPT_BODY",BODY,{"disambiguationData":[OSD([sQuery(id+"F2.wireOp",EDGE,"E20.9.7.0"),sQuery(id+"F2.wireOp",EDGE,"E20.12.7.0"),sQuery(id+"F2.wireOp",EDGE,"E20.15.7.0")])]});
            var Q55;
            Q55=makeQuery(id+"F4.opExtrude","SWEPT_BODY",BODY,{"disambiguationData":[OSD([sQuery(id+"F2.wireOp",EDGE,"E20.0.7.0"),sQuery(id+"F2.wireOp",EDGE,"E20.3.7.0"),sQuery(id+"F2.wireOp",EDGE,"E20.6.7.0")])]});
            var Q56;
            Q56=makeQuery(id+"F4.opExtrude","SWEPT_BODY",BODY,{"disambiguationData":[OSD([sQuery(id+"F2.wireOp",EDGE,"E20.27.6.0"),sQuery(id+"F2.wireOp",EDGE,"E20.30.6.0"),sQuery(id+"F2.wireOp",EDGE,"E20.33.6.0")])]});
            var Q57;
            Q57=makeQuery(id+"F4.opExtrude","SWEPT_BODY",BODY,{"disambiguationData":[OSD([sQuery(id+"F2.wireOp",EDGE,"E20.18.6.0"),sQuery(id+"F2.wireOp",EDGE,"E20.21.6.0"),sQuery(id+"F2.wireOp",EDGE,"E20.24.6.0")])]});
            var Q58;
            Q58=makeQuery(id+"F4.opExtrude","SWEPT_BODY",BODY,{"disambiguationData":[OSD([sQuery(id+"F2.wireOp",EDGE,"E20.9.6.0"),sQuery(id+"F2.wireOp",EDGE,"E20.12.6.0"),sQuery(id+"F2.wireOp",EDGE,"E20.15.6.0")])]});
            var Q59;
            Q59=makeQuery(id+"F4.opExtrude","SWEPT_BODY",BODY,{"disambiguationData":[OSD([sQuery(id+"F2.wireOp",EDGE,"E20.0.6.0"),sQuery(id+"F2.wireOp",EDGE,"E20.3.6.0"),sQuery(id+"F2.wireOp",EDGE,"E20.6.6.0")])]});
            var Q60;
            Q60=makeQuery(id+"F4.opExtrude","SWEPT_BODY",BODY,{"disambiguationData":[OSD([sQuery(id+"F2.wireOp",EDGE,"E20.27.5.0"),sQuery(id+"F2.wireOp",EDGE,"E20.30.5.0"),sQuery(id+"F2.wireOp",EDGE,"E20.33.5.0")])]});
            var Q61;
            Q61=makeQuery(id+"F4.opExtrude","SWEPT_BODY",BODY,{"disambiguationData":[OSD([sQuery(id+"F2.wireOp",EDGE,"E20.18.5.0"),sQuery(id+"F2.wireOp",EDGE,"E20.21.5.0"),sQuery(id+"F2.wireOp",EDGE,"E20.24.5.0")])]});
            var Q62;
            Q62=makeQuery(id+"F4.opExtrude","SWEPT_BODY",BODY,{"disambiguationData":[OSD([sQuery(id+"F2.wireOp",EDGE,"E20.9.5.0"),sQuery(id+"F2.wireOp",EDGE,"E20.12.5.0"),sQuery(id+"F2.wireOp",EDGE,"E20.15.5.0")])]});
            var Q63;
            Q63=makeQuery(id+"F4.opExtrude","SWEPT_BODY",BODY,{"disambiguationData":[OSD([sQuery(id+"F2.wireOp",EDGE,"E20.0.5.0"),sQuery(id+"F2.wireOp",EDGE,"E20.3.5.0"),sQuery(id+"F2.wireOp",EDGE,"E20.6.5.0")])]});
            var Q64;
            Q64=makeQuery(id+"F4.opExtrude","SWEPT_BODY",BODY,{"disambiguationData":[OSD([sQuery(id+"F2.wireOp",EDGE,"E19.27.4.0"),sQuery(id+"F2.wireOp",EDGE,"E19.30.4.0"),sQuery(id+"F2.wireOp",EDGE,"E19.33.4.0")])]});
            var Q65;
            Q65=makeQuery(id+"F4.opExtrude","SWEPT_BODY",BODY,{"disambiguationData":[OSD([sQuery(id+"F2.wireOp",EDGE,"E19.18.4.0"),sQuery(id+"F2.wireOp",EDGE,"E19.21.4.0"),sQuery(id+"F2.wireOp",EDGE,"E19.24.4.0")])]});
            var Q66;
            Q66=makeQuery(id+"F4.opExtrude","SWEPT_BODY",BODY,{"disambiguationData":[OSD([sQuery(id+"F2.wireOp",EDGE,"E19.9.4.0"),sQuery(id+"F2.wireOp",EDGE,"E19.12.4.0"),sQuery(id+"F2.wireOp",EDGE,"E19.15.4.0")])]});
            var Q67;
            Q67=makeQuery(id+"F4.opExtrude","SWEPT_BODY",BODY,{"disambiguationData":[OSD([sQuery(id+"F2.wireOp",EDGE,"E19.0.4.0"),sQuery(id+"F2.wireOp",EDGE,"E19.3.4.0"),sQuery(id+"F2.wireOp",EDGE,"E19.6.4.0")])]});
            var Q68;
            Q68=makeQuery(id+"F4.opExtrude","SWEPT_BODY",BODY,{"disambiguationData":[OSD([sQuery(id+"F2.wireOp",EDGE,"E19.27.3.0"),sQuery(id+"F2.wireOp",EDGE,"E19.30.3.0"),sQuery(id+"F2.wireOp",EDGE,"E19.33.3.0")])]});
            var Q69;
            Q69=makeQuery(id+"F4.opExtrude","SWEPT_BODY",BODY,{"disambiguationData":[OSD([sQuery(id+"F2.wireOp",EDGE,"E19.18.3.0"),sQuery(id+"F2.wireOp",EDGE,"E19.21.3.0"),sQuery(id+"F2.wireOp",EDGE,"E19.24.3.0")])]});
            var Q70;
            Q70=makeQuery(id+"F4.opExtrude","SWEPT_BODY",BODY,{"disambiguationData":[OSD([sQuery(id+"F2.wireOp",EDGE,"E19.9.3.0"),sQuery(id+"F2.wireOp",EDGE,"E19.12.3.0"),sQuery(id+"F2.wireOp",EDGE,"E19.15.3.0")])]});
            var Q71;
            Q71=makeQuery(id+"F4.opExtrude","SWEPT_BODY",BODY,{"disambiguationData":[OSD([sQuery(id+"F2.wireOp",EDGE,"E19.0.3.0"),sQuery(id+"F2.wireOp",EDGE,"E19.3.3.0"),sQuery(id+"F2.wireOp",EDGE,"E19.6.3.0")])]});
            var Q72;
            Q72=makeQuery(id+"F4.opExtrude","SWEPT_BODY",BODY,{"disambiguationData":[OSD([sQuery(id+"F2.wireOp",EDGE,"E18.2.0.9"),sQuery(id+"F2.wireOp",EDGE,"E18.2.0.10"),sQuery(id+"F2.wireOp",EDGE,"E18.2.0.11")])]});
            var Q73;
            Q73=makeQuery(id+"F4.opExtrude","SWEPT_BODY",BODY,{"disambiguationData":[OSD([sQuery(id+"F2.wireOp",EDGE,"E18.2.0.6"),sQuery(id+"F2.wireOp",EDGE,"E18.2.0.7"),sQuery(id+"F2.wireOp",EDGE,"E18.2.0.8")])]});
            var Q74;
            Q74=makeQuery(id+"F4.opExtrude","SWEPT_BODY",BODY,{"disambiguationData":[OSD([sQuery(id+"F2.wireOp",EDGE,"E18.2.0.3"),sQuery(id+"F2.wireOp",EDGE,"E18.2.0.4"),sQuery(id+"F2.wireOp",EDGE,"E18.2.0.5")])]});
            var Q75;
            Q75=makeQuery(id+"F4.opExtrude","SWEPT_BODY",BODY,{"disambiguationData":[OSD([sQuery(id+"F2.wireOp",EDGE,"E18.2.0.0"),sQuery(id+"F2.wireOp",EDGE,"E18.2.0.1"),sQuery(id+"F2.wireOp",EDGE,"E18.2.0.2")])]});
            var Q76;
            Q76=makeQuery(id+"F4.opExtrude","SWEPT_BODY",BODY,{"disambiguationData":[OSD([sQuery(id+"F2.wireOp",EDGE,"E18.1.0.9"),sQuery(id+"F2.wireOp",EDGE,"E18.1.0.10"),sQuery(id+"F2.wireOp",EDGE,"E18.1.0.11")])]});
            var Q77;
            Q77=makeQuery(id+"F4.opExtrude","SWEPT_BODY",BODY,{"disambiguationData":[OSD([sQuery(id+"F2.wireOp",EDGE,"E18.1.0.6"),sQuery(id+"F2.wireOp",EDGE,"E18.1.0.7"),sQuery(id+"F2.wireOp",EDGE,"E18.1.0.8")])]});
            var Q78;
            Q78=makeQuery(id+"F4.opExtrude","SWEPT_BODY",BODY,{"disambiguationData":[OSD([sQuery(id+"F2.wireOp",EDGE,"E18.1.0.3"),sQuery(id+"F2.wireOp",EDGE,"E18.1.0.4"),sQuery(id+"F2.wireOp",EDGE,"E18.1.0.5")])]});
            var Q79;
            Q79=makeQuery(id+"F4.opExtrude","SWEPT_BODY",BODY,{"disambiguationData":[OSD([sQuery(id+"F2.wireOp",EDGE,"E18.1.0.0"),sQuery(id+"F2.wireOp",EDGE,"E18.1.0.1"),sQuery(id+"F2.wireOp",EDGE,"E18.1.0.2")])]});
            var Q80;
            Q80=makeQuery(id+"F4.opExtrude","SWEPT_BODY",BODY,{"disambiguationData":[OSD([sQuery(id+"F2.wireOp",EDGE,"E5.5"),sQuery(id+"F2.wireOp",EDGE,"E12.trimOffspring"),sQuery(id+"F2.wireOp",EDGE,"E16.trimOffspring")])]});
            var Q81;
            Q81=makeQuery(id+"F4.opExtrude","SWEPT_BODY",BODY,{"disambiguationData":[OSD([sQuery(id+"F2.wireOp",EDGE,"E5.4"),sQuery(id+"F2.wireOp",EDGE,"E15.trimOffspring"),sQuery(id+"F2.wireOp",EDGE,"E17.trimOffspring")])]});
            var Q82;
            Q82=makeQuery(id+"F4.opExtrude","SWEPT_BODY",BODY,{"disambiguationData":[OSD([sQuery(id+"F2.wireOp",EDGE,"E5.3"),sQuery(id+"F2.wireOp",EDGE,"E9.0"),sQuery(id+"F2.wireOp",EDGE,"E11.trimOffspring")])]});
            var Q83;
            Q83=makeQuery(id+"F4.opExtrude","SWEPT_BODY",BODY,{"disambiguationData":[OSD([sQuery(id+"F2.wireOp",EDGE,"E5.0"),sQuery(id+"F2.wireOp",EDGE,"E8.0"),sQuery(id+"F2.wireOp",EDGE,"E14.trimOffspring")])]});
            var Q84;
            Q84=makeQuery(id+"F4.opExtrude","SWEPT_BODY",BODY,{"disambiguationData":[OSD([sQuery(id+"F2.wireOp",EDGE,"E5.1"),sQuery(id+"F2.wireOp",EDGE,"E6.0"),sQuery(id+"F2.wireOp",EDGE,"E10.trimOffspring")])]});
            var Q85;
            Q85=makeQuery(id+"F4.opExtrude","SWEPT_BODY",BODY,{"disambiguationData":[OSD([sQuery(id+"F2.wireOp",EDGE,"E5.2"),sQuery(id+"F2.wireOp",EDGE,"E7.0"),sQuery(id+"F2.wireOp",EDGE,"E13.trimOffspring")])]});
            var Q86;
            Q86=makeQuery(id+"F1.opExtrude","SWEPT_BODY",BODY,{"disambiguationData":[OSD([sQuery(id+"F0.wireOp",EDGE,"E0.bottom"),sQuery(id+"F0.wireOp",EDGE,"E0.top"),sQuery(id+"F0.wireOp",EDGE,"E0.left"),sQuery(id+"F0.wireOp",EDGE,"E0.right")])]});
            booleanBodies(context, id + "F6", {"operationType" : BooleanOperationType.SUBTRACTION, "tools" : qUnion([Q0, Q1, Q2, Q3, Q4, Q5, Q6, Q7, Q8, Q9, Q10, Q11, Q12, Q13, Q14, Q15, Q16, Q17, Q18, Q19, Q20, Q21, Q22, Q23, Q24, Q25, Q26, Q27, Q28, Q29, Q30, Q31, Q32, Q33, Q34, Q35, Q36, Q37, Q38, Q39, Q40, Q41, Q42, Q43, Q44, Q45, Q46, Q47, Q48, Q49, Q50, Q51, Q52, Q53, Q54, Q55, Q56, Q57, Q58, Q59, Q60, Q61, Q62, Q63, Q64, Q65, Q66, Q67, Q68, Q69, Q70, Q71, Q72, Q73, Q74, Q75, Q76, Q77, Q78, Q79, Q80, Q81, Q82, Q83, Q84, Q85]), "targets" : qUnion([Q86])});
        }
    });
